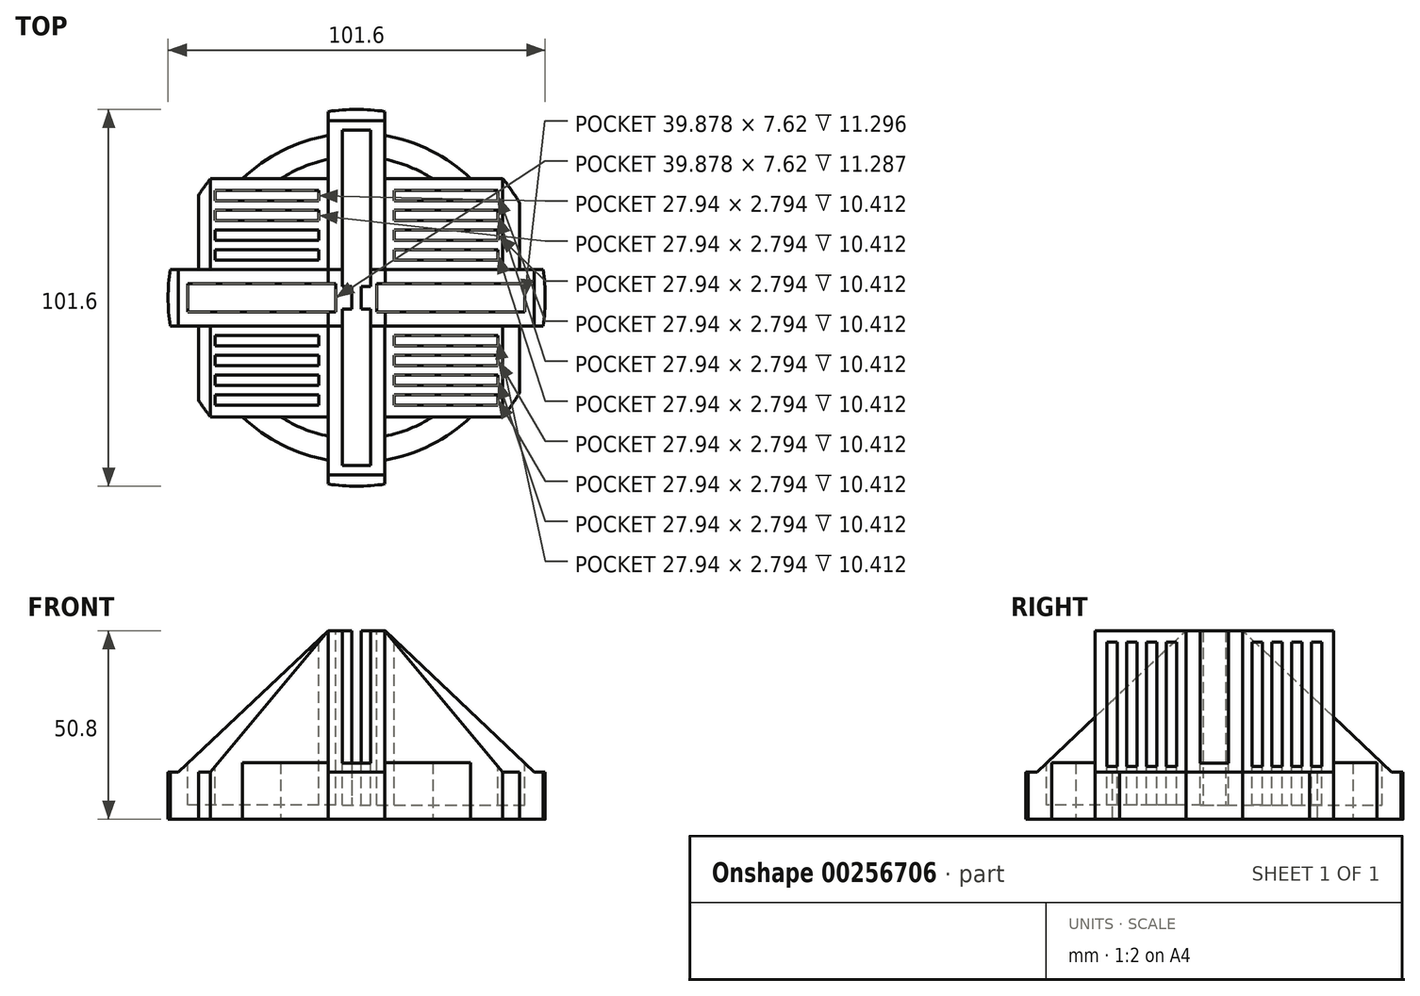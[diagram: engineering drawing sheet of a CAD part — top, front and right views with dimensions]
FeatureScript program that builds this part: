
annotation { "Feature Type Name" : "Feature", "Feature Type Description" : "" }
export const myFeature = defineFeature(function(context is Context, id is Id, definition is map)
    precondition{}
    {
        {
            var Q0;
            Q0=qCreatedBy(makeId("Top.planeOp"),FACE);
            cPlane(context, id + "F0", {"entities" : qUnion([Q0]), "cplaneType" : CPlaneType.OFFSET, "offset" : 50.8 * mm, "width" : 152.4 * mm, "height" : 152.4 * mm});
        }
        {
            var Q0;
            Q0=qCreatedBy(makeId("Top.planeOp"),FACE);
            var sketch = newSketch(context, id + "F1", { "sketchPlane" : qUnion([Q0])});
            skCircle(sketch, "E0", {"center": v(0, 0) * mm, "radius": 50.8 * mm});
            skArc(sketch, "E1", {"start": v(7.62, -43.8) * mm, "mid": v(26.54, -35.66) * mm, "end": v(39.77, -19.86) * mm});
            skArc(sketch, "E2", {"start": v(7.62, -37.33) * mm, "mid": v(38.1, 0) * mm, "end": v(7.62, 37.33) * mm});
            skCircle(sketch, "E3", {"center": v(0, 0) * mm, "radius": 25.4 * mm});
            skLineSegment(sketch, "E4", {"start": v(-7.62, -24.23) * mm, "end": v(-7.62, -50.23) * mm});
            skLineSegment(sketch, "E5", {"start": v(7.62, -24.23) * mm, "end": v(7.62, -50.23) * mm});
            skLineSegment(sketch, "E6", {"start": v(-7.62, 24.23) * mm, "end": v(-7.62, 50.23) * mm});
            skLineSegment(sketch, "E7", {"start": v(7.62, 24.23) * mm, "end": v(7.62, 50.23) * mm});
            skPoint(sketch, "E8.orphan", {"position": v(0, -25.4) * mm});
            skPoint(sketch, "E9.end.orphan", {"position": v(-3.8, -50.66) * mm});
            skArc(sketch, "E10.trimOffspring", {"start": v(-7.62, 37.33) * mm, "mid": v(-38.1, 0) * mm, "end": v(-7.62, -37.33) * mm});
            skArc(sketch, "E11.trimOffspring", {"start": v(-7.62, 43.8) * mm, "mid": v(-26.54, 35.66) * mm, "end": v(-39.77, 19.86) * mm});
            skArc(sketch, "E12", {"start": v(-7.62, -43.8) * mm, "mid": v(0, -44.45) * mm, "end": v(7.62, -43.8) * mm});
            skArc(sketch, "E13", {"start": v(-7.62, -37.33) * mm, "mid": v(0, -38.1) * mm, "end": v(7.62, -37.33) * mm});
            skCircle(sketch, "E14", {"center": v(0, 0) * mm, "radius": 31.75 * mm});
            skArc(sketch, "E15.trimOffspring", {"start": v(7.62, 43.8) * mm, "mid": v(0, 44.45) * mm, "end": v(-7.62, 43.8) * mm});
            skArc(sketch, "E16.trimOffspring", {"start": v(7.62, 37.33) * mm, "mid": v(0, 38.1) * mm, "end": v(-7.62, 37.33) * mm});
            skLineSegment(sketch, "E17", {"start": v(-7.62, -24.23) * mm, "end": v(-7.62, 24.23) * mm});
            skLineSegment(sketch, "E18", {"start": v(7.62, 24.23) * mm, "end": v(7.62, -24.23) * mm});
            skLineSegment(sketch, "E19", {"start": v(0, 7.62) * mm, "end": v(-50.23, 7.62) * mm});
            skLineSegment(sketch, "E20", {"start": v(0, 7.62) * mm, "end": v(50.23, 7.62) * mm});
            skLineSegment(sketch, "E21", {"start": v(0, -7.62) * mm, "end": v(50.23, -7.62) * mm});
            skLineSegment(sketch, "E22", {"start": v(0, -7.62) * mm, "end": v(-50.23, -7.62) * mm});
            skLineSegment(sketch, "E23", {"start": v(-17.78, 7.62) * mm, "end": v(7.62, -17.78) * mm});
            skLineSegment(sketch, "E24", {"start": v(-7.62, 17.78) * mm, "end": v(17.78, -7.62) * mm});
            skLineSegment(sketch, "E25", {"start": v(7.62, 17.78) * mm, "end": v(-17.78, -7.62) * mm});
            skLineSegment(sketch, "E26", {"start": v(17.78, 7.62) * mm, "end": v(-7.62, -17.78) * mm});
            skLineSegment(sketch, "E27", {"start": v(-7.62, -19.86) * mm, "end": v(-20.32, -19.86) * mm});
            skLineSegment(sketch, "E28", {"start": v(-20.32, -19.86) * mm, "end": v(-46.76, -19.86) * mm});
            skLineSegment(sketch, "E29.trimOffspring", {"start": v(-20.32, -32.1) * mm, "end": v(-20.32, -32.23) * mm});
            skPoint(sketch, "E30.start.orphan", {"position": v(-20.32, -7.62) * mm});
            skLineSegment(sketch, "E31", {"start": v(-7.62, -32.1) * mm, "end": v(-39.37, -32.1) * mm});
            skLineSegment(sketch, "E32", {"start": v(-7.62, 19.86) * mm, "end": v(-46.76, 19.86) * mm});
            skLineSegment(sketch, "E33", {"start": v(-7.62, 32.1) * mm, "end": v(-39.37, 32.1) * mm});
            skLineSegment(sketch, "E34", {"start": v(7.62, 32.1) * mm, "end": v(39.37, 32.1) * mm});
            skLineSegment(sketch, "E35", {"start": v(7.62, 19.86) * mm, "end": v(46.76, 19.86) * mm});
            skLineSegment(sketch, "E36", {"start": v(7.62, -19.86) * mm, "end": v(46.76, -19.86) * mm});
            skLineSegment(sketch, "E37", {"start": v(7.62, -32.1) * mm, "end": v(39.37, -32.1) * mm});
            skLineSegment(sketch, "E38", {"start": v(-42.64, 19.86) * mm, "end": v(-42.64, -19.86) * mm});
            skArc(sketch, "E39.trimOffspring", {"start": v(-39.77, -19.86) * mm, "mid": v(-26.54, -35.66) * mm, "end": v(-7.62, -43.8) * mm});
            skLineSegment(sketch, "E40", {"start": v(43.89, -19.86) * mm, "end": v(43.89, 19.86) * mm});
            skArc(sketch, "E41.trimOffspring", {"start": v(39.77, 19.86) * mm, "mid": v(26.54, 35.66) * mm, "end": v(7.62, 43.8) * mm});
            skSolve(sketch);
        }
        {
            var Q0;
            {var subQ5=sQuery(id+"F1.wireOp",EDGE,"E15.trimOffspring");Q0=makeQuery(id+"F1.imprint","IMPRINT",FACE,{"disambiguationData":[TD([[makeQuery(id+"F1.imprint","IMPRINT",EDGE,{"derivedFrom":subQ5}),-1.0]])]});}
            var Q1;
            {var subQ5=sQuery(id+"F1.wireOp",EDGE,"E12");Q1=makeQuery(id+"F1.imprint","IMPRINT",FACE,{"disambiguationData":[TD([[makeQuery(id+"F1.imprint","IMPRINT",EDGE,{"derivedFrom":subQ5}),-1.0]])]});}
            var Q2;
            {var subQ0=sQuery(id+"F1.wireOp",EDGE,"E32");var subQ6=sQuery(id+"F1.wireOp",EDGE,"E0");var subQ7=makeQuery(id+"F1.imprint","INTERSECT",VERTEX,{"derivedFrom":[subQ6,subQ0]});Q2=makeQuery(id+"F1.imprint","IMPRINT",FACE,{"disambiguationData":[TD([[makeQuery(id+"F1.imprint","IMPRINT",EDGE,{"disambiguationData":[TD([[subQ7,1.0]])],"derivedFrom":subQ6}),1.0]])]});}
            var Q3;
            {var subQ0=sQuery(id+"F1.wireOp",EDGE,"E19");var subQ1=sQuery(id+"F1.wireOp",EDGE,"E0");var subQ2=makeQuery(id+"F1.imprint","INTERSECT",VERTEX,{"derivedFrom":[subQ1,subQ0]});Q3=makeQuery(id+"F1.imprint","IMPRINT",FACE,{"disambiguationData":[TD([[makeQuery(id+"F1.imprint","IMPRINT",EDGE,{"disambiguationData":[TD([[subQ2,1.0]])],"derivedFrom":subQ1}),1.0]])]});}
            var Q4;
            {var subQ0=sQuery(id+"F1.wireOp",EDGE,"E19");var subQ1=sQuery(id+"F1.wireOp",EDGE,"E0");var subQ2=makeQuery(id+"F1.imprint","INTERSECT",VERTEX,{"derivedFrom":[subQ1,subQ0]});Q4=makeQuery(id+"F1.imprint","IMPRINT",FACE,{"disambiguationData":[TD([[makeQuery(id+"F1.imprint","IMPRINT",EDGE,{"disambiguationData":[TD([[subQ2,-1.0]])],"derivedFrom":subQ1}),1.0]])]});}
            var Q5;
            {var subQ0=sQuery(id+"F1.wireOp",EDGE,"E22");var subQ1=sQuery(id+"F1.wireOp",EDGE,"E0");var subQ2=makeQuery(id+"F1.imprint","INTERSECT",VERTEX,{"derivedFrom":[subQ1,subQ0]});Q5=makeQuery(id+"F1.imprint","IMPRINT",FACE,{"disambiguationData":[TD([[makeQuery(id+"F1.imprint","IMPRINT",EDGE,{"disambiguationData":[TD([[subQ2,-1.0]])],"derivedFrom":subQ1}),1.0]])]});}
            var Q6;
            {var subQ0=sQuery(id+"F1.wireOp",EDGE,"E28");var subQ4=sQuery(id+"F1.wireOp",EDGE,"E0");var subQ5=makeQuery(id+"F1.imprint","INTERSECT",VERTEX,{"derivedFrom":[subQ4,subQ0]});Q6=makeQuery(id+"F1.imprint","IMPRINT",FACE,{"disambiguationData":[TD([[makeQuery(id+"F1.imprint","IMPRINT",EDGE,{"disambiguationData":[TD([[subQ5,-1.0]])],"derivedFrom":subQ4}),1.0]])]});}
            var Q7;
            {var subQ1=sQuery(id+"F1.wireOp",EDGE,"E0");var subQ6=sQuery(id+"F1.wireOp",EDGE,"E34");var subQ8=makeQuery(id+"F1.imprint","INTERSECT",VERTEX,{"derivedFrom":[subQ1,subQ6]});Q7=makeQuery(id+"F1.imprint","IMPRINT",FACE,{"disambiguationData":[TD([[makeQuery(id+"F1.imprint","IMPRINT",EDGE,{"disambiguationData":[TD([[subQ8,1.0]])],"derivedFrom":subQ1}),1.0]])]});}
            var Q8;
            {var subQ0=sQuery(id+"F1.wireOp",EDGE,"E20");var subQ1=sQuery(id+"F1.wireOp",EDGE,"E0");var subQ2=makeQuery(id+"F1.imprint","INTERSECT",VERTEX,{"derivedFrom":[subQ1,subQ0]});Q8=makeQuery(id+"F1.imprint","IMPRINT",FACE,{"disambiguationData":[TD([[makeQuery(id+"F1.imprint","IMPRINT",EDGE,{"disambiguationData":[TD([[subQ2,-1.0]])],"derivedFrom":subQ1}),1.0]])]});}
            var Q9;
            {var subQ1=sQuery(id+"F1.wireOp",EDGE,"E0");var subQ5=sQuery(id+"F1.wireOp",EDGE,"E20");var subQ6=makeQuery(id+"F1.imprint","INTERSECT",VERTEX,{"derivedFrom":[subQ1,subQ5]});Q9=makeQuery(id+"F1.imprint","IMPRINT",FACE,{"disambiguationData":[TD([[makeQuery(id+"F1.imprint","IMPRINT",EDGE,{"disambiguationData":[TD([[subQ6,1.0]])],"derivedFrom":subQ1}),1.0]])]});}
            var Q10;
            {var subQ0=sQuery(id+"F1.wireOp",EDGE,"E21");var subQ1=sQuery(id+"F1.wireOp",EDGE,"E0");var subQ2=makeQuery(id+"F1.imprint","INTERSECT",VERTEX,{"derivedFrom":[subQ1,subQ0]});Q10=makeQuery(id+"F1.imprint","IMPRINT",FACE,{"disambiguationData":[TD([[makeQuery(id+"F1.imprint","IMPRINT",EDGE,{"disambiguationData":[TD([[subQ2,1.0]])],"derivedFrom":subQ1}),1.0]])]});}
            var Q11;
            {var subQ0=sQuery(id+"F1.wireOp",EDGE,"E36");var subQ1=sQuery(id+"F1.wireOp",EDGE,"E0");var subQ2=makeQuery(id+"F1.imprint","INTERSECT",VERTEX,{"derivedFrom":[subQ1,subQ0]});Q11=makeQuery(id+"F1.imprint","IMPRINT",FACE,{"disambiguationData":[TD([[makeQuery(id+"F1.imprint","IMPRINT",EDGE,{"disambiguationData":[TD([[subQ2,1.0]])],"derivedFrom":subQ1}),1.0]])]});}
            var Q12;
            {var subQ0=sQuery(id+"F1.wireOp",EDGE,"E4");var subQ1=sQuery(id+"F1.wireOp",EDGE,"E0");var subQ2=makeQuery(id+"F1.imprint","INTERSECT",VERTEX,{"derivedFrom":[subQ1,subQ0]});Q12=makeQuery(id+"F1.imprint","IMPRINT",FACE,{"disambiguationData":[TD([[makeQuery(id+"F1.imprint","IMPRINT",EDGE,{"disambiguationData":[TD([[subQ2,1.0]])],"derivedFrom":subQ1}),1.0]])]});}
            var Q13;
            {var subQ0=sQuery(id+"F1.wireOp",EDGE,"E6");var subQ1=sQuery(id+"F1.wireOp",EDGE,"E0");var subQ2=makeQuery(id+"F1.imprint","INTERSECT",VERTEX,{"derivedFrom":[subQ1,subQ0]});Q13=makeQuery(id+"F1.imprint","IMPRINT",FACE,{"disambiguationData":[TD([[makeQuery(id+"F1.imprint","IMPRINT",EDGE,{"disambiguationData":[TD([[subQ2,-1.0]])],"derivedFrom":subQ1}),1.0]])]});}
            var Q14;
            {var subQ0=sQuery(id+"F1.wireOp",EDGE,"E7");var subQ1=sQuery(id+"F1.wireOp",EDGE,"E0");var subQ2=makeQuery(id+"F1.imprint","INTERSECT",VERTEX,{"derivedFrom":[subQ1,subQ0]});Q14=makeQuery(id+"F1.imprint","IMPRINT",FACE,{"disambiguationData":[TD([[makeQuery(id+"F1.imprint","IMPRINT",EDGE,{"disambiguationData":[TD([[subQ2,1.0]])],"derivedFrom":subQ1}),1.0]])]});}
            var Q15;
            {var subQ0=sQuery(id+"F1.wireOp",EDGE,"E5");var subQ1=sQuery(id+"F1.wireOp",EDGE,"E0");var subQ2=makeQuery(id+"F1.imprint","INTERSECT",VERTEX,{"derivedFrom":[subQ1,subQ0]});Q15=makeQuery(id+"F1.imprint","IMPRINT",FACE,{"disambiguationData":[TD([[makeQuery(id+"F1.imprint","IMPRINT",EDGE,{"disambiguationData":[TD([[subQ2,-1.0]])],"derivedFrom":subQ1}),1.0]])]});}
            extrude(context, id + "F2", {"entities" : qUnion([Q0, Q1, Q2, Q3, Q4, Q5, Q6, Q7, Q8, Q9, Q10, Q11, Q12, Q13, Q14, Q15]), "depth" : 12.7 * mm});
        }
        {
            var Q0;
            {var subQ0=sQuery(id+"F1.wireOp",EDGE,"E10.trimOffspring");Q0=makeQuery(id+"F1.imprint","IMPRINT",FACE,{"disambiguationData":[TD([[makeQuery(id+"F1.imprint","IMPRINT",EDGE,{"derivedFrom":subQ0}),-1.0]])]});}
            var Q1;
            {var subQ0=sQuery(id+"F1.wireOp",EDGE,"E1");Q1=makeQuery(id+"F1.imprint","IMPRINT",FACE,{"disambiguationData":[TD([[makeQuery(id+"F1.imprint","IMPRINT",EDGE,{"derivedFrom":subQ0}),1.0]])]});}
            var Q2;
            {var subQ2=sQuery(id+"F1.wireOp",EDGE,"E15.trimOffspring");Q2=makeQuery(id+"F1.imprint","IMPRINT",FACE,{"disambiguationData":[TD([[makeQuery(id+"F1.imprint","IMPRINT",EDGE,{"derivedFrom":subQ2}),1.0]])]});}
            var Q3;
            {var subQ2=sQuery(id+"F1.wireOp",EDGE,"E12");Q3=makeQuery(id+"F1.imprint","IMPRINT",FACE,{"disambiguationData":[TD([[makeQuery(id+"F1.imprint","IMPRINT",EDGE,{"derivedFrom":subQ2}),1.0]])]});}
            var Q4;
            {var subQ0=sQuery(id+"F1.wireOp",EDGE,"E10.trimOffspring");var subQ5=sQuery(id+"F1.wireOp",EDGE,"KU0cdiGB-8eOj-Trs3-v5YD-3LzdnCRRimhK");var subQ6=makeQuery(id+"F1.imprint","INTERSECT",VERTEX,{"derivedFrom":[subQ0,subQ5]});Q4=makeQuery(id+"F1.imprint","IMPRINT",FACE,{"disambiguationData":[TD([[makeQuery(id+"F1.imprint","IMPRINT",EDGE,{"disambiguationData":[TD([[subQ6,-1.0]])],"derivedFrom":subQ5}),-1.0]])]});}
            var Q5;
            {var subQ0=sQuery(id+"F1.wireOp",EDGE,"KU0cdiGB-8eOj-Trs3-v5YD-3LzdnCRRimhK");var subQ1=sQuery(id+"F1.wireOp",EDGE,"E10.trimOffspring");var subQ2=makeQuery(id+"F1.imprint","INTERSECT",VERTEX,{"derivedFrom":[subQ1,subQ0]});Q5=makeQuery(id+"F1.imprint","IMPRINT",FACE,{"disambiguationData":[TD([[makeQuery(id+"F1.imprint","IMPRINT",EDGE,{"disambiguationData":[TD([[subQ2,-1.0]])],"derivedFrom":subQ1}),-1.0]])]});}
            var Q6;
            {var subQ0=sQuery(id+"F1.wireOp",EDGE,"n5LII22h-w08l-qE72-yfr9-18N67uZxNTdQ");var subQ1=sQuery(id+"F1.wireOp",EDGE,"E10.trimOffspring");var subQ2=makeQuery(id+"F1.imprint","INTERSECT",VERTEX,{"derivedFrom":[subQ1,subQ0]});Q6=makeQuery(id+"F1.imprint","IMPRINT",FACE,{"disambiguationData":[TD([[makeQuery(id+"F1.imprint","IMPRINT",EDGE,{"disambiguationData":[TD([[subQ2,-1.0]])],"derivedFrom":subQ1}),-1.0]])]});}
            var Q7;
            {var subQ0=sQuery(id+"F1.wireOp",EDGE,"E19");var subQ1=sQuery(id+"F1.wireOp",EDGE,"E10.trimOffspring");var subQ2=makeQuery(id+"F1.imprint","INTERSECT",VERTEX,{"derivedFrom":[subQ1,subQ0]});Q7=makeQuery(id+"F1.imprint","IMPRINT",FACE,{"disambiguationData":[TD([[makeQuery(id+"F1.imprint","IMPRINT",EDGE,{"disambiguationData":[TD([[subQ2,-1.0]])],"derivedFrom":subQ1}),-1.0]])]});}
            var Q8;
            {var subQ0=sQuery(id+"F1.wireOp",EDGE,"E22");var subQ1=sQuery(id+"F1.wireOp",EDGE,"E10.trimOffspring");var subQ2=makeQuery(id+"F1.imprint","INTERSECT",VERTEX,{"derivedFrom":[subQ1,subQ0]});Q8=makeQuery(id+"F1.imprint","IMPRINT",FACE,{"disambiguationData":[TD([[makeQuery(id+"F1.imprint","IMPRINT",EDGE,{"disambiguationData":[TD([[subQ2,-1.0]])],"derivedFrom":subQ1}),-1.0]])]});}
            var Q9;
            {var subQ0=sQuery(id+"F1.wireOp",EDGE,"E28");var subQ1=sQuery(id+"F1.wireOp",EDGE,"E10.trimOffspring");var subQ2=makeQuery(id+"F1.imprint","INTERSECT",VERTEX,{"derivedFrom":[subQ1,subQ0]});Q9=makeQuery(id+"F1.imprint","IMPRINT",FACE,{"disambiguationData":[TD([[makeQuery(id+"F1.imprint","IMPRINT",EDGE,{"disambiguationData":[TD([[subQ2,-1.0]])],"derivedFrom":subQ1}),-1.0]])]});}
            var Q10;
            {var subQ1=sQuery(id+"F1.wireOp",EDGE,"E10.trimOffspring");var subQ5=sQuery(id+"F1.wireOp",EDGE,"E25");var subQ6=makeQuery(id+"F1.imprint","INTERSECT",VERTEX,{"derivedFrom":[subQ1,subQ5]});Q10=makeQuery(id+"F1.imprint","IMPRINT",FACE,{"disambiguationData":[TD([[makeQuery(id+"F1.imprint","IMPRINT",EDGE,{"disambiguationData":[TD([[subQ6,-1.0]])],"derivedFrom":subQ1}),-1.0]])]});}
            var Q11;
            {var subQ0=sQuery(id+"F1.wireOp",EDGE,"E31");var subQ1=sQuery(id+"F1.wireOp",EDGE,"E11.trimOffspring");var subQ2=makeQuery(id+"F1.imprint","INTERSECT",VERTEX,{"derivedFrom":[subQ1,subQ0]});Q11=makeQuery(id+"F1.imprint","IMPRINT",FACE,{"disambiguationData":[TD([[makeQuery(id+"F1.imprint","IMPRINT",EDGE,{"disambiguationData":[TD([[subQ2,-1.0]])],"derivedFrom":subQ1}),1.0]])]});}
            var Q12;
            {var subQ0=sQuery(id+"F1.wireOp",EDGE,"E26");var subQ1=sQuery(id+"F1.wireOp",EDGE,"E10.trimOffspring");var subQ2=makeQuery(id+"F1.imprint","INTERSECT",VERTEX,{"derivedFrom":[subQ1,subQ0]});Q12=makeQuery(id+"F1.imprint","IMPRINT",FACE,{"disambiguationData":[TD([[makeQuery(id+"F1.imprint","IMPRINT",EDGE,{"disambiguationData":[TD([[subQ2,-1.0]])],"derivedFrom":subQ1}),-1.0]])]});}
            var Q13;
            {var subQ0=sQuery(id+"F1.wireOp",EDGE,"E32");var subQ1=sQuery(id+"F1.wireOp",EDGE,"E10.trimOffspring");var subQ2=makeQuery(id+"F1.imprint","INTERSECT",VERTEX,{"derivedFrom":[subQ1,subQ0]});Q13=makeQuery(id+"F1.imprint","IMPRINT",FACE,{"disambiguationData":[TD([[makeQuery(id+"F1.imprint","IMPRINT",EDGE,{"disambiguationData":[TD([[subQ2,-1.0]])],"derivedFrom":subQ1}),-1.0]])]});}
            var Q14;
            {var subQ0=sQuery(id+"F1.wireOp",EDGE,"E33");var subQ1=sQuery(id+"F1.wireOp",EDGE,"E10.trimOffspring");var subQ2=makeQuery(id+"F1.imprint","INTERSECT",VERTEX,{"derivedFrom":[subQ1,subQ0]});Q14=makeQuery(id+"F1.imprint","IMPRINT",FACE,{"disambiguationData":[TD([[makeQuery(id+"F1.imprint","IMPRINT",EDGE,{"disambiguationData":[TD([[subQ2,-1.0]])],"derivedFrom":subQ1}),-1.0]])]});}
            var Q15;
            {var subQ0=sQuery(id+"F1.wireOp",EDGE,"E10.trimOffspring");var subQ5=sQuery(id+"F1.wireOp",EDGE,"E33");var subQ7=makeQuery(id+"F1.imprint","INTERSECT",VERTEX,{"derivedFrom":[subQ0,subQ5]});Q15=makeQuery(id+"F1.imprint","IMPRINT",FACE,{"disambiguationData":[TD([[makeQuery(id+"F1.imprint","IMPRINT",EDGE,{"disambiguationData":[TD([[subQ7,-1.0]])],"derivedFrom":subQ5}),-1.0]])]});}
            var Q16;
            {var subQ0=sQuery(id+"F1.wireOp",EDGE,"E35");var subQ1=sQuery(id+"F1.wireOp",EDGE,"E2");var subQ2=makeQuery(id+"F1.imprint","INTERSECT",VERTEX,{"derivedFrom":[subQ1,subQ0]});Q16=makeQuery(id+"F1.imprint","IMPRINT",FACE,{"disambiguationData":[TD([[makeQuery(id+"F1.imprint","IMPRINT",EDGE,{"disambiguationData":[TD([[subQ2,-1.0]])],"derivedFrom":subQ1}),-1.0]])]});}
            var Q17;
            {var subQ0=sQuery(id+"F1.wireOp",EDGE,"E20");var subQ6=sQuery(id+"F1.wireOp",EDGE,"E2");var subQ8=makeQuery(id+"F1.imprint","INTERSECT",VERTEX,{"derivedFrom":[subQ6,subQ0]});Q17=makeQuery(id+"F1.imprint","IMPRINT",FACE,{"disambiguationData":[TD([[makeQuery(id+"F1.imprint","IMPRINT",EDGE,{"disambiguationData":[TD([[subQ8,-1.0]])],"derivedFrom":subQ6}),-1.0]])]});}
            var Q18;
            {var subQ0=sQuery(id+"F1.wireOp",EDGE,"18cd6810-feed-407b-96fd-876ede30ebc9.trimOffspring");Q18=makeQuery(id+"F1.imprint","IMPRINT",FACE,{"disambiguationData":[TD([[makeQuery(id+"F1.imprint","IMPRINT",EDGE,{"derivedFrom":subQ0}),1.0]])]});}
            var Q19;
            {var subQ0=sQuery(id+"F1.wireOp",EDGE,"E36");var subQ2=sQuery(id+"F1.wireOp",EDGE,"E2");var subQ3=makeQuery(id+"F1.imprint","INTERSECT",VERTEX,{"derivedFrom":[subQ2,subQ0]});Q19=makeQuery(id+"F1.imprint","IMPRINT",FACE,{"disambiguationData":[TD([[makeQuery(id+"F1.imprint","IMPRINT",EDGE,{"disambiguationData":[TD([[subQ3,-1.0]])],"derivedFrom":subQ2}),-1.0]])]});}
            var Q20;
            {var subQ0=sQuery(id+"F1.wireOp",EDGE,"E21");var subQ1=sQuery(id+"F1.wireOp",EDGE,"E2");var subQ2=makeQuery(id+"F1.imprint","INTERSECT",VERTEX,{"derivedFrom":[subQ1,subQ0]});Q20=makeQuery(id+"F1.imprint","IMPRINT",FACE,{"disambiguationData":[TD([[makeQuery(id+"F1.imprint","IMPRINT",EDGE,{"disambiguationData":[TD([[subQ2,-1.0]])],"derivedFrom":subQ1}),-1.0]])]});}
            var Q21;
            {var subQ1=sQuery(id+"F1.wireOp",EDGE,"E2");var subQ3=sQuery(id+"F1.wireOp",EDGE,"E34");var subQ4=makeQuery(id+"F1.imprint","INTERSECT",VERTEX,{"derivedFrom":[subQ1,subQ3]});Q21=makeQuery(id+"F1.imprint","IMPRINT",FACE,{"disambiguationData":[TD([[makeQuery(id+"F1.imprint","IMPRINT",EDGE,{"disambiguationData":[TD([[subQ4,-1.0]])],"derivedFrom":subQ3}),1.0]])]});}
            extrude(context, id + "F3", {"entities" : qUnion([Q0, Q1, Q2, Q3, Q4, Q5, Q6, Q7, Q8, Q9, Q10, Q11, Q12, Q13, Q14, Q15, Q16, Q17, Q18, Q19, Q20, Q21]), "operationType" : NewBodyOperationType.ADD, "depth" : 25.4 * mm});
        }
        {
            var Q0;
            {var subQ0=sQuery(id+"F1.wireOp",EDGE,"E13");Q0=makeQuery(id+"F1.imprint","IMPRINT",FACE,{"disambiguationData":[TD([[makeQuery(id+"F1.imprint","IMPRINT",EDGE,{"derivedFrom":subQ0}),1.0]])]});}
            var Q1;
            {var subQ0=sQuery(id+"F1.wireOp",EDGE,"E10.trimOffspring");Q1=makeQuery(id+"F1.imprint","IMPRINT",FACE,{"disambiguationData":[TD([[makeQuery(id+"F1.imprint","IMPRINT",EDGE,{"derivedFrom":subQ0}),1.0]])]});}
            var Q2;
            {var subQ0=sQuery(id+"F1.wireOp",EDGE,"E2");Q2=makeQuery(id+"F1.imprint","IMPRINT",FACE,{"disambiguationData":[TD([[makeQuery(id+"F1.imprint","IMPRINT",EDGE,{"derivedFrom":subQ0}),1.0]])]});}
            var Q3;
            {var subQ0=sQuery(id+"F1.wireOp",EDGE,"E16.trimOffspring");Q3=makeQuery(id+"F1.imprint","IMPRINT",FACE,{"disambiguationData":[TD([[makeQuery(id+"F1.imprint","IMPRINT",EDGE,{"derivedFrom":subQ0}),1.0]])]});}
            var Q4;
            {var subQ0=sQuery(id+"F1.wireOp",EDGE,"n5LII22h-w08l-qE72-yfr9-18N67uZxNTdQ");var subQ1=sQuery(id+"F1.wireOp",EDGE,"E10.trimOffspring");var subQ2=makeQuery(id+"F1.imprint","INTERSECT",VERTEX,{"derivedFrom":[subQ1,subQ0]});Q4=makeQuery(id+"F1.imprint","IMPRINT",FACE,{"disambiguationData":[TD([[makeQuery(id+"F1.imprint","IMPRINT",EDGE,{"disambiguationData":[TD([[subQ2,-1.0]])],"derivedFrom":subQ1}),1.0]])]});}
            var Q5;
            {var subQ0=sQuery(id+"F1.wireOp",EDGE,"KU0cdiGB-8eOj-Trs3-v5YD-3LzdnCRRimhK");var subQ1=sQuery(id+"F1.wireOp",EDGE,"E10.trimOffspring");var subQ2=makeQuery(id+"F1.imprint","INTERSECT",VERTEX,{"derivedFrom":[subQ1,subQ0]});Q5=makeQuery(id+"F1.imprint","IMPRINT",FACE,{"disambiguationData":[TD([[makeQuery(id+"F1.imprint","IMPRINT",EDGE,{"disambiguationData":[TD([[subQ2,-1.0]])],"derivedFrom":subQ1}),1.0]])]});}
            var Q6;
            {var subQ1=sQuery(id+"F1.wireOp",EDGE,"E6");var subQ3=sQuery(id+"F1.wireOp",EDGE,"E14");var subQ4=makeQuery(id+"F1.imprint","INTERSECT",VERTEX,{"derivedFrom":[subQ1,subQ3]});Q6=makeQuery(id+"F1.imprint","IMPRINT",FACE,{"disambiguationData":[TD([[makeQuery(id+"F1.imprint","IMPRINT",EDGE,{"disambiguationData":[TD([[subQ4,-1.0]])],"derivedFrom":subQ3}),-1.0]])]});}
            var Q7;
            {var subQ0=sQuery(id+"F1.wireOp",EDGE,"E7");var subQ5=sQuery(id+"F1.wireOp",EDGE,"E14");var subQ6=makeQuery(id+"F1.imprint","INTERSECT",VERTEX,{"derivedFrom":[subQ0,subQ5]});Q7=makeQuery(id+"F1.imprint","IMPRINT",FACE,{"disambiguationData":[TD([[makeQuery(id+"F1.imprint","IMPRINT",EDGE,{"disambiguationData":[TD([[subQ6,1.0]])],"derivedFrom":subQ5}),-1.0]])]});}
            var Q8;
            {var subQ0=sQuery(id+"F1.wireOp",EDGE,"E19");var subQ1=sQuery(id+"F1.wireOp",EDGE,"E10.trimOffspring");var subQ2=makeQuery(id+"F1.imprint","INTERSECT",VERTEX,{"derivedFrom":[subQ1,subQ0]});Q8=makeQuery(id+"F1.imprint","IMPRINT",FACE,{"disambiguationData":[TD([[makeQuery(id+"F1.imprint","IMPRINT",EDGE,{"disambiguationData":[TD([[subQ2,-1.0]])],"derivedFrom":subQ1}),1.0]])]});}
            var Q9;
            {var subQ0=sQuery(id+"F1.wireOp",EDGE,"E22");var subQ1=sQuery(id+"F1.wireOp",EDGE,"E10.trimOffspring");var subQ2=makeQuery(id+"F1.imprint","INTERSECT",VERTEX,{"derivedFrom":[subQ1,subQ0]});Q9=makeQuery(id+"F1.imprint","IMPRINT",FACE,{"disambiguationData":[TD([[makeQuery(id+"F1.imprint","IMPRINT",EDGE,{"disambiguationData":[TD([[subQ2,-1.0]])],"derivedFrom":subQ1}),1.0]])]});}
            var Q10;
            {var subQ0=sQuery(id+"F1.wireOp",EDGE,"E25");var subQ1=sQuery(id+"F1.wireOp",EDGE,"E10.trimOffspring");var subQ2=makeQuery(id+"F1.imprint","INTERSECT",VERTEX,{"derivedFrom":[subQ1,subQ0]});Q10=makeQuery(id+"F1.imprint","IMPRINT",FACE,{"disambiguationData":[TD([[makeQuery(id+"F1.imprint","IMPRINT",EDGE,{"disambiguationData":[TD([[subQ2,-1.0]])],"derivedFrom":subQ1}),1.0]])]});}
            var Q11;
            {var subQ3=sQuery(id+"F1.wireOp",EDGE,"E14");var subQ7=sQuery(id+"F1.wireOp",EDGE,"E4");var subQ8=makeQuery(id+"F1.imprint","INTERSECT",VERTEX,{"derivedFrom":[subQ7,subQ3]});Q11=makeQuery(id+"F1.imprint","IMPRINT",FACE,{"disambiguationData":[TD([[makeQuery(id+"F1.imprint","IMPRINT",EDGE,{"disambiguationData":[TD([[subQ8,-1.0]])],"derivedFrom":subQ7}),-1.0]])]});}
            var Q12;
            {var subQ1=sQuery(id+"F1.wireOp",EDGE,"E2");var subQ5=sQuery(id+"F1.wireOp",EDGE,"dChad7VG-r3lr-Y0ra-zuCQ-UW0r8UzcO7aT");var subQ6=makeQuery(id+"F1.imprint","INTERSECT",VERTEX,{"derivedFrom":[subQ1,subQ5]});Q12=makeQuery(id+"F1.imprint","IMPRINT",FACE,{"disambiguationData":[TD([[makeQuery(id+"F1.imprint","IMPRINT",EDGE,{"disambiguationData":[TD([[subQ6,-1.0]])],"derivedFrom":subQ1}),1.0]])]});}
            var Q13;
            {var subQ0=sQuery(id+"F1.wireOp",EDGE,"E23");var subQ1=sQuery(id+"F1.wireOp",EDGE,"E2");var subQ2=makeQuery(id+"F1.imprint","INTERSECT",VERTEX,{"derivedFrom":[subQ1,subQ0]});Q13=makeQuery(id+"F1.imprint","IMPRINT",FACE,{"disambiguationData":[TD([[makeQuery(id+"F1.imprint","IMPRINT",EDGE,{"disambiguationData":[TD([[subQ2,-1.0]])],"derivedFrom":subQ1}),1.0]])]});}
            var Q14;
            {var subQ0=sQuery(id+"F1.wireOp",EDGE,"E24");var subQ1=sQuery(id+"F1.wireOp",EDGE,"E2");var subQ2=makeQuery(id+"F1.imprint","INTERSECT",VERTEX,{"derivedFrom":[subQ1,subQ0]});Q14=makeQuery(id+"F1.imprint","IMPRINT",FACE,{"disambiguationData":[TD([[makeQuery(id+"F1.imprint","IMPRINT",EDGE,{"disambiguationData":[TD([[subQ2,-1.0]])],"derivedFrom":subQ1}),1.0]])]});}
            var Q15;
            {var subQ0=sQuery(id+"F1.wireOp",EDGE,"E21");var subQ1=sQuery(id+"F1.wireOp",EDGE,"E2");var subQ2=makeQuery(id+"F1.imprint","INTERSECT",VERTEX,{"derivedFrom":[subQ1,subQ0]});Q15=makeQuery(id+"F1.imprint","IMPRINT",FACE,{"disambiguationData":[TD([[makeQuery(id+"F1.imprint","IMPRINT",EDGE,{"disambiguationData":[TD([[subQ2,-1.0]])],"derivedFrom":subQ1}),1.0]])]});}
            var Q16;
            {var subQ0=sQuery(id+"F1.wireOp",EDGE,"E20");var subQ1=sQuery(id+"F1.wireOp",EDGE,"E2");var subQ2=makeQuery(id+"F1.imprint","INTERSECT",VERTEX,{"derivedFrom":[subQ1,subQ0]});Q16=makeQuery(id+"F1.imprint","IMPRINT",FACE,{"disambiguationData":[TD([[makeQuery(id+"F1.imprint","IMPRINT",EDGE,{"disambiguationData":[TD([[subQ2,-1.0]])],"derivedFrom":subQ1}),1.0]])]});}
            var Q17;
            {var subQ0=sQuery(id+"F1.wireOp",EDGE,"SVIod6WE-LFFt-Ms97-owyS-8ShU65W6W8it");var subQ1=sQuery(id+"F1.wireOp",EDGE,"E2");var subQ2=makeQuery(id+"F1.imprint","INTERSECT",VERTEX,{"derivedFrom":[subQ1,subQ0]});Q17=makeQuery(id+"F1.imprint","IMPRINT",FACE,{"disambiguationData":[TD([[makeQuery(id+"F1.imprint","IMPRINT",EDGE,{"disambiguationData":[TD([[subQ2,-1.0]])],"derivedFrom":subQ1}),1.0]])]});}
            var Q18;
            {var subQ0=sQuery(id+"F1.wireOp",EDGE,"E25");var subQ1=sQuery(id+"F1.wireOp",EDGE,"E14");var subQ2=makeQuery(id+"F1.imprint","INTERSECT",VERTEX,{"derivedFrom":[subQ1,subQ0]});Q18=makeQuery(id+"F1.imprint","IMPRINT",FACE,{"disambiguationData":[TD([[makeQuery(id+"F1.imprint","IMPRINT",EDGE,{"disambiguationData":[TD([[subQ2,-1.0]])],"derivedFrom":subQ1}),-1.0]])]});}
            var Q19;
            {var subQ0=sQuery(id+"F1.wireOp",EDGE,"E30");var subQ1=sQuery(id+"F1.wireOp",EDGE,"E14");var subQ2=makeQuery(id+"F1.imprint","INTERSECT",VERTEX,{"derivedFrom":[subQ1,subQ0]});Q19=makeQuery(id+"F1.imprint","IMPRINT",FACE,{"disambiguationData":[TD([[makeQuery(id+"F1.imprint","IMPRINT",EDGE,{"disambiguationData":[TD([[subQ2,-1.0]])],"derivedFrom":subQ1}),-1.0]])]});}
            var Q20;
            {var subQ5=sQuery(id+"F1.wireOp",EDGE,"E29.trimOffspring");Q20=makeQuery(id+"F1.imprint","IMPRINT",FACE,{"disambiguationData":[TD([[makeQuery(id+"F1.imprint","IMPRINT",EDGE,{"derivedFrom":subQ5}),1.0]])]});}
            var Q21;
            {var subQ1=sQuery(id+"F1.wireOp",EDGE,"E2");var subQ7=sQuery(id+"F1.wireOp",EDGE,"E37");var subQ9=makeQuery(id+"F1.imprint","INTERSECT",VERTEX,{"derivedFrom":[subQ1,subQ7]});Q21=makeQuery(id+"F1.imprint","IMPRINT",FACE,{"disambiguationData":[TD([[makeQuery(id+"F1.imprint","IMPRINT",EDGE,{"disambiguationData":[TD([[subQ9,-1.0]])],"derivedFrom":subQ1}),1.0]])]});}
            extrude(context, id + "F4", {"entities" : qUnion([Q0, Q1, Q2, Q3, Q4, Q5, Q6, Q7, Q8, Q9, Q10, Q11, Q12, Q13, Q14, Q15, Q16, Q17, Q18, Q19, Q20, Q21]), "operationType" : NewBodyOperationType.ADD, "depth" : 38.1 * mm});
        }
        {
            var Q0;
            {var subQ0=sQuery(id+"F1.wireOp",EDGE,"E6");var subQ1=sQuery(id+"F1.wireOp",EDGE,"E3");var subQ2=makeQuery(id+"F1.imprint","INTERSECT",VERTEX,{"derivedFrom":[subQ1,subQ0]});Q0=makeQuery(id+"F1.imprint","IMPRINT",FACE,{"disambiguationData":[TD([[makeQuery(id+"F1.imprint","IMPRINT",EDGE,{"disambiguationData":[TD([[subQ2,1.0]])],"derivedFrom":subQ1}),-1.0]])]});}
            var Q1;
            {var subQ0=sQuery(id+"F1.wireOp",EDGE,"E4");var subQ1=sQuery(id+"F1.wireOp",EDGE,"E3");var subQ2=makeQuery(id+"F1.imprint","INTERSECT",VERTEX,{"derivedFrom":[subQ1,subQ0]});Q1=makeQuery(id+"F1.imprint","IMPRINT",FACE,{"disambiguationData":[TD([[makeQuery(id+"F1.imprint","IMPRINT",EDGE,{"disambiguationData":[TD([[subQ2,-1.0]])],"derivedFrom":subQ1}),-1.0]])]});}
            var Q2;
            {var subQ0=sQuery(id+"F1.wireOp",EDGE,"E5");var subQ1=sQuery(id+"F1.wireOp",EDGE,"E3");var subQ2=makeQuery(id+"F1.imprint","INTERSECT",VERTEX,{"derivedFrom":[subQ1,subQ0]});Q2=makeQuery(id+"F1.imprint","IMPRINT",FACE,{"disambiguationData":[TD([[makeQuery(id+"F1.imprint","IMPRINT",EDGE,{"disambiguationData":[TD([[subQ2,-1.0]])],"derivedFrom":subQ1}),-1.0]])]});}
            var Q3;
            {var subQ0=sQuery(id+"F1.wireOp",EDGE,"E7");var subQ5=sQuery(id+"F1.wireOp",EDGE,"E14");var subQ6=makeQuery(id+"F1.imprint","INTERSECT",VERTEX,{"derivedFrom":[subQ0,subQ5]});Q3=makeQuery(id+"F1.imprint","IMPRINT",FACE,{"disambiguationData":[TD([[makeQuery(id+"F1.imprint","IMPRINT",EDGE,{"disambiguationData":[TD([[subQ6,1.0]])],"derivedFrom":subQ5}),1.0]])]});}
            var Q4;
            {var subQ0=sQuery(id+"F1.wireOp",EDGE,"E19");var subQ1=sQuery(id+"F1.wireOp",EDGE,"E3");var subQ2=makeQuery(id+"F1.imprint","INTERSECT",VERTEX,{"derivedFrom":[subQ1,subQ0]});Q4=makeQuery(id+"F1.imprint","IMPRINT",FACE,{"disambiguationData":[TD([[makeQuery(id+"F1.imprint","IMPRINT",EDGE,{"disambiguationData":[TD([[subQ2,-1.0]])],"derivedFrom":subQ1}),-1.0]])]});}
            var Q5;
            {var subQ0=sQuery(id+"F1.wireOp",EDGE,"E6");var subQ5=sQuery(id+"F1.wireOp",EDGE,"E14");var subQ6=makeQuery(id+"F1.imprint","INTERSECT",VERTEX,{"derivedFrom":[subQ0,subQ5]});Q5=makeQuery(id+"F1.imprint","IMPRINT",FACE,{"disambiguationData":[TD([[makeQuery(id+"F1.imprint","IMPRINT",EDGE,{"disambiguationData":[TD([[subQ6,-1.0]])],"derivedFrom":subQ5}),1.0]])]});}
            var Q6;
            {var subQ0=sQuery(id+"F1.wireOp",EDGE,"E20");var subQ1=sQuery(id+"F1.wireOp",EDGE,"E3");var subQ2=makeQuery(id+"F1.imprint","INTERSECT",VERTEX,{"derivedFrom":[subQ1,subQ0]});Q6=makeQuery(id+"F1.imprint","IMPRINT",FACE,{"disambiguationData":[TD([[makeQuery(id+"F1.imprint","IMPRINT",EDGE,{"disambiguationData":[TD([[subQ2,1.0]])],"derivedFrom":subQ1}),-1.0]])]});}
            var Q7;
            {var subQ1=sQuery(id+"F1.wireOp",EDGE,"E4");var subQ3=sQuery(id+"F1.wireOp",EDGE,"E14");var subQ4=makeQuery(id+"F1.imprint","INTERSECT",VERTEX,{"derivedFrom":[subQ1,subQ3]});Q7=makeQuery(id+"F1.imprint","IMPRINT",FACE,{"disambiguationData":[TD([[makeQuery(id+"F1.imprint","IMPRINT",EDGE,{"disambiguationData":[TD([[subQ4,1.0]])],"derivedFrom":subQ3}),1.0]])]});}
            var Q8;
            {var subQ3=sQuery(id+"F1.wireOp",EDGE,"6cIBHAnO-3Gdr-gs2R-q8mb-qejxkHO2rhEE");var subQ5=sQuery(id+"F1.wireOp",EDGE,"E14");var subQ6=makeQuery(id+"F1.imprint","INTERSECT",VERTEX,{"derivedFrom":[subQ5,subQ3]});Q8=makeQuery(id+"F1.imprint","IMPRINT",FACE,{"disambiguationData":[TD([[makeQuery(id+"F1.imprint","IMPRINT",EDGE,{"disambiguationData":[TD([[subQ6,-1.0]])],"derivedFrom":subQ5}),1.0]])]});}
            var Q9;
            {var subQ0=sQuery(id+"F1.wireOp",EDGE,"E22");var subQ1=sQuery(id+"F1.wireOp",EDGE,"E14");var subQ2=makeQuery(id+"F1.imprint","INTERSECT",VERTEX,{"derivedFrom":[subQ1,subQ0]});Q9=makeQuery(id+"F1.imprint","IMPRINT",FACE,{"disambiguationData":[TD([[makeQuery(id+"F1.imprint","IMPRINT",EDGE,{"disambiguationData":[TD([[subQ2,-1.0]])],"derivedFrom":subQ1}),1.0]])]});}
            var Q10;
            {var subQ3=sQuery(id+"F1.wireOp",EDGE,"1679b663-5bbc-411f-b373-dbe6ce103e45.trimOffspring");var subQ5=sQuery(id+"F1.wireOp",EDGE,"E14");var subQ7=makeQuery(id+"F1.imprint","INTERSECT",VERTEX,{"disambiguationData":[OD(1.0)],"derivedFrom":[subQ5,subQ3]});Q10=makeQuery(id+"F1.imprint","IMPRINT",FACE,{"disambiguationData":[TD([[makeQuery(id+"F1.imprint","IMPRINT",EDGE,{"disambiguationData":[TD([[subQ7,-1.0]])],"derivedFrom":subQ5}),1.0]])]});}
            var Q11;
            {var subQ3=sQuery(id+"F1.wireOp",EDGE,"8l5Dcz2D-qY2G-ceuh-glFK-kLwJx8DI5XpU");var subQ5=sQuery(id+"F1.wireOp",EDGE,"E14");var subQ7=makeQuery(id+"F1.imprint","INTERSECT",VERTEX,{"derivedFrom":[subQ5,subQ3]});Q11=makeQuery(id+"F1.imprint","IMPRINT",FACE,{"disambiguationData":[TD([[makeQuery(id+"F1.imprint","IMPRINT",EDGE,{"disambiguationData":[TD([[subQ7,-1.0]])],"derivedFrom":subQ5}),1.0]])]});}
            var Q12;
            {var subQ0=sQuery(id+"F1.wireOp",EDGE,"n5LII22h-w08l-qE72-yfr9-18N67uZxNTdQ");var subQ1=sQuery(id+"F1.wireOp",EDGE,"E3");var subQ2=makeQuery(id+"F1.imprint","INTERSECT",VERTEX,{"derivedFrom":[subQ1,subQ0]});Q12=makeQuery(id+"F1.imprint","IMPRINT",FACE,{"disambiguationData":[TD([[makeQuery(id+"F1.imprint","IMPRINT",EDGE,{"disambiguationData":[TD([[subQ2,-1.0]])],"derivedFrom":subQ1}),-1.0]])]});}
            var Q13;
            {var subQ0=sQuery(id+"F1.wireOp",EDGE,"KU0cdiGB-8eOj-Trs3-v5YD-3LzdnCRRimhK");var subQ1=sQuery(id+"F1.wireOp",EDGE,"E3");var subQ2=makeQuery(id+"F1.imprint","INTERSECT",VERTEX,{"derivedFrom":[subQ1,subQ0]});Q13=makeQuery(id+"F1.imprint","IMPRINT",FACE,{"disambiguationData":[TD([[makeQuery(id+"F1.imprint","IMPRINT",EDGE,{"disambiguationData":[TD([[subQ2,-1.0]])],"derivedFrom":subQ1}),-1.0]])]});}
            var Q14;
            {var subQ0=sQuery(id+"F1.wireOp",EDGE,"SVIod6WE-LFFt-Ms97-owyS-8ShU65W6W8it");var subQ1=sQuery(id+"F1.wireOp",EDGE,"E3");var subQ2=makeQuery(id+"F1.imprint","INTERSECT",VERTEX,{"derivedFrom":[subQ1,subQ0]});Q14=makeQuery(id+"F1.imprint","IMPRINT",FACE,{"disambiguationData":[TD([[makeQuery(id+"F1.imprint","IMPRINT",EDGE,{"disambiguationData":[TD([[subQ2,-1.0]])],"derivedFrom":subQ1}),-1.0]])]});}
            var Q15;
            {var subQ0=sQuery(id+"F1.wireOp",EDGE,"SVIod6WE-LFFt-Ms97-owyS-8ShU65W6W8it");var subQ1=sQuery(id+"F1.wireOp",EDGE,"E3");var subQ2=makeQuery(id+"F1.imprint","INTERSECT",VERTEX,{"derivedFrom":[subQ1,subQ0]});Q15=makeQuery(id+"F1.imprint","IMPRINT",FACE,{"disambiguationData":[TD([[makeQuery(id+"F1.imprint","IMPRINT",EDGE,{"disambiguationData":[TD([[subQ2,1.0]])],"derivedFrom":subQ1}),-1.0]])]});}
            var Q16;
            {var subQ0=sQuery(id+"F1.wireOp",EDGE,"E24");var subQ1=sQuery(id+"F1.wireOp",EDGE,"E3");var subQ2=makeQuery(id+"F1.imprint","INTERSECT",VERTEX,{"derivedFrom":[subQ1,subQ0]});Q16=makeQuery(id+"F1.imprint","IMPRINT",FACE,{"disambiguationData":[TD([[makeQuery(id+"F1.imprint","IMPRINT",EDGE,{"disambiguationData":[TD([[subQ2,-1.0]])],"derivedFrom":subQ1}),-1.0]])]});}
            var Q17;
            {var subQ0=sQuery(id+"F1.wireOp",EDGE,"E23");var subQ1=sQuery(id+"F1.wireOp",EDGE,"E3");var subQ2=makeQuery(id+"F1.imprint","INTERSECT",VERTEX,{"derivedFrom":[subQ1,subQ0]});Q17=makeQuery(id+"F1.imprint","IMPRINT",FACE,{"disambiguationData":[TD([[makeQuery(id+"F1.imprint","IMPRINT",EDGE,{"disambiguationData":[TD([[subQ2,-1.0]])],"derivedFrom":subQ1}),-1.0]])]});}
            var Q18;
            {var subQ1=sQuery(id+"F1.wireOp",EDGE,"E27");var subQ3=sQuery(id+"F1.wireOp",EDGE,"E3");var subQ4=makeQuery(id+"F1.imprint","INTERSECT",VERTEX,{"derivedFrom":[subQ3,subQ1]});Q18=makeQuery(id+"F1.imprint","IMPRINT",FACE,{"disambiguationData":[TD([[makeQuery(id+"F1.imprint","IMPRINT",EDGE,{"disambiguationData":[TD([[subQ4,-1.0]])],"derivedFrom":subQ3}),-1.0]])]});}
            var Q19;
            {var subQ0=sQuery(id+"F1.wireOp",EDGE,"E30");var subQ1=sQuery(id+"F1.wireOp",EDGE,"E3");var subQ2=makeQuery(id+"F1.imprint","INTERSECT",VERTEX,{"derivedFrom":[subQ1,subQ0]});Q19=makeQuery(id+"F1.imprint","IMPRINT",FACE,{"disambiguationData":[TD([[makeQuery(id+"F1.imprint","IMPRINT",EDGE,{"disambiguationData":[TD([[subQ2,-1.0]])],"derivedFrom":subQ1}),-1.0]])]});}
            var Q20;
            {var subQ0=sQuery(id+"F1.wireOp",EDGE,"E25");var subQ7=sQuery(id+"F1.wireOp",EDGE,"E3");var subQ8=makeQuery(id+"F1.imprint","INTERSECT",VERTEX,{"derivedFrom":[subQ7,subQ0]});Q20=makeQuery(id+"F1.imprint","IMPRINT",FACE,{"disambiguationData":[TD([[makeQuery(id+"F1.imprint","IMPRINT",EDGE,{"disambiguationData":[TD([[subQ8,-1.0]])],"derivedFrom":subQ7}),-1.0]])]});}
            extrude(context, id + "F5", {"entities" : qUnion([Q0, Q1, Q2, Q3, Q4, Q5, Q6, Q7, Q8, Q9, Q10, Q11, Q12, Q13, Q14, Q15, Q16, Q17, Q18, Q19, Q20]), "operationType" : NewBodyOperationType.ADD, "depth" : 50.8 * mm});
        }
        {
            var Q0;
            {var subQ5=sQuery(id+"F1.wireOp",EDGE,"E12");Q0=makeQuery(id+"F1.imprint","IMPRINT",FACE,{"disambiguationData":[TD([[makeQuery(id+"F1.imprint","IMPRINT",EDGE,{"derivedFrom":subQ5}),-1.0]])]});}
            var Q1;
            {var subQ0=sQuery(id+"F1.wireOp",EDGE,"E13");Q1=makeQuery(id+"F1.imprint","IMPRINT",FACE,{"disambiguationData":[TD([[makeQuery(id+"F1.imprint","IMPRINT",EDGE,{"derivedFrom":subQ0}),1.0]])]});}
            var Q2;
            {var subQ0=sQuery(id+"F1.wireOp",EDGE,"E4");var subQ1=sQuery(id+"F1.wireOp",EDGE,"E3");var subQ2=makeQuery(id+"F1.imprint","INTERSECT",VERTEX,{"derivedFrom":[subQ1,subQ0]});Q2=makeQuery(id+"F1.imprint","IMPRINT",FACE,{"disambiguationData":[TD([[makeQuery(id+"F1.imprint","IMPRINT",EDGE,{"disambiguationData":[TD([[subQ2,-1.0]])],"derivedFrom":subQ1}),-1.0]])]});}
            var Q3;
            {var subQ2=sQuery(id+"F1.wireOp",EDGE,"E12");Q3=makeQuery(id+"F1.imprint","IMPRINT",FACE,{"disambiguationData":[TD([[makeQuery(id+"F1.imprint","IMPRINT",EDGE,{"derivedFrom":subQ2}),1.0]])]});}
            var Q4;
            {var subQ0=sQuery(id+"F1.wireOp",EDGE,"E17");Q4=makeQuery(id+"F1.imprint","IMPRINT",FACE,{"disambiguationData":[TD([[makeQuery(id+"F1.imprint","IMPRINT",EDGE,{"derivedFrom":subQ0}),-1.0]])]});}
            var Q5;
            {var subQ0=sQuery(id+"F1.wireOp",EDGE,"E6");var subQ5=sQuery(id+"F1.wireOp",EDGE,"E14");var subQ6=makeQuery(id+"F1.imprint","INTERSECT",VERTEX,{"derivedFrom":[subQ0,subQ5]});Q5=makeQuery(id+"F1.imprint","IMPRINT",FACE,{"disambiguationData":[TD([[makeQuery(id+"F1.imprint","IMPRINT",EDGE,{"disambiguationData":[TD([[subQ6,1.0]])],"derivedFrom":subQ5}),1.0]])]});}
            var Q6;
            {var subQ0=sQuery(id+"F1.wireOp",EDGE,"E16.trimOffspring");Q6=makeQuery(id+"F1.imprint","IMPRINT",FACE,{"disambiguationData":[TD([[makeQuery(id+"F1.imprint","IMPRINT",EDGE,{"derivedFrom":subQ0}),1.0]])]});}
            var Q7;
            {var subQ2=sQuery(id+"F1.wireOp",EDGE,"E15.trimOffspring");Q7=makeQuery(id+"F1.imprint","IMPRINT",FACE,{"disambiguationData":[TD([[makeQuery(id+"F1.imprint","IMPRINT",EDGE,{"derivedFrom":subQ2}),1.0]])]});}
            var Q8;
            {var subQ5=sQuery(id+"F1.wireOp",EDGE,"E15.trimOffspring");Q8=makeQuery(id+"F1.imprint","IMPRINT",FACE,{"disambiguationData":[TD([[makeQuery(id+"F1.imprint","IMPRINT",EDGE,{"derivedFrom":subQ5}),-1.0]])]});}
            var Q9;
            {var subQ0=sQuery(id+"F1.wireOp",EDGE,"8l5Dcz2D-qY2G-ceuh-glFK-kLwJx8DI5XpU");var subQ3=sQuery(id+"F1.wireOp",EDGE,"E18");var subQ5=makeQuery(id+"F1.imprint","INTERSECT",VERTEX,{"derivedFrom":[subQ3,subQ0]});Q9=makeQuery(id+"F1.imprint","IMPRINT",FACE,{"disambiguationData":[TD([[makeQuery(id+"F1.imprint","IMPRINT",EDGE,{"disambiguationData":[TD([[subQ5,-1.0]])],"derivedFrom":subQ3}),-1.0]])]});}
            var Q10;
            {var subQ1=sQuery(id+"F1.wireOp",EDGE,"E21");var subQ5=sQuery(id+"F1.wireOp",EDGE,"E18");var subQ6=makeQuery(id+"F1.imprint","INTERSECT",VERTEX,{"derivedFrom":[subQ5,subQ1]});Q10=makeQuery(id+"F1.imprint","IMPRINT",FACE,{"disambiguationData":[TD([[makeQuery(id+"F1.imprint","IMPRINT",EDGE,{"disambiguationData":[TD([[subQ6,-1.0]])],"derivedFrom":subQ5}),-1.0]])]});}
            var Q11;
            {var subQ1=sQuery(id+"F1.wireOp",EDGE,"E19");var subQ7=sQuery(id+"F1.wireOp",EDGE,"E17");var subQ8=makeQuery(id+"F1.imprint","INTERSECT",VERTEX,{"derivedFrom":[subQ7,subQ1]});Q11=makeQuery(id+"F1.imprint","IMPRINT",FACE,{"disambiguationData":[TD([[makeQuery(id+"F1.imprint","IMPRINT",EDGE,{"disambiguationData":[TD([[subQ8,-1.0]])],"derivedFrom":subQ7}),-1.0]])]});}
            var Q12;
            {var subQ3=sQuery(id+"F1.wireOp",EDGE,"E17");var subQ9=sQuery(id+"F1.wireOp",EDGE,"E22");var subQ10=makeQuery(id+"F1.imprint","INTERSECT",VERTEX,{"derivedFrom":[subQ3,subQ9]});Q12=makeQuery(id+"F1.imprint","IMPRINT",FACE,{"disambiguationData":[TD([[makeQuery(id+"F1.imprint","IMPRINT",EDGE,{"disambiguationData":[TD([[subQ10,-1.0]])],"derivedFrom":subQ3}),-1.0]])]});}
            var Q13;
            {var subQ0=sQuery(id+"F1.wireOp",EDGE,"E22");var subQ1=sQuery(id+"F1.wireOp",EDGE,"E17");var subQ2=makeQuery(id+"F1.imprint","INTERSECT",VERTEX,{"derivedFrom":[subQ1,subQ0]});Q13=makeQuery(id+"F1.imprint","IMPRINT",FACE,{"disambiguationData":[TD([[makeQuery(id+"F1.imprint","IMPRINT",EDGE,{"disambiguationData":[TD([[subQ2,1.0]])],"derivedFrom":subQ0}),1.0]])]});}
            var Q14;
            {var subQ3=sQuery(id+"F1.wireOp",EDGE,"E17");var subQ11=sQuery(id+"F1.wireOp",EDGE,"E23");var subQ12=makeQuery(id+"F1.imprint","INTERSECT",VERTEX,{"derivedFrom":[subQ3,subQ11]});Q14=makeQuery(id+"F1.imprint","IMPRINT",FACE,{"disambiguationData":[TD([[makeQuery(id+"F1.imprint","IMPRINT",EDGE,{"disambiguationData":[TD([[subQ12,-1.0]])],"derivedFrom":subQ3}),-1.0]])]});}
            var Q15;
            {var subQ0=sQuery(id+"F1.wireOp",EDGE,"E20");var subQ1=sQuery(id+"F1.wireOp",EDGE,"E18");var subQ2=makeQuery(id+"F1.imprint","INTERSECT",VERTEX,{"derivedFrom":[subQ1,subQ0]});Q15=makeQuery(id+"F1.imprint","IMPRINT",FACE,{"disambiguationData":[TD([[makeQuery(id+"F1.imprint","IMPRINT",EDGE,{"disambiguationData":[TD([[subQ2,1.0]])],"derivedFrom":subQ0}),1.0]])]});}
            var Q16;
            {var subQ0=sQuery(id+"F1.wireOp",EDGE,"E18");var subQ3=sQuery(id+"F1.wireOp",EDGE,"E23");var subQ4=makeQuery(id+"F1.imprint","INTERSECT",VERTEX,{"derivedFrom":[subQ0,subQ3]});Q16=makeQuery(id+"F1.imprint","IMPRINT",FACE,{"disambiguationData":[TD([[makeQuery(id+"F1.imprint","IMPRINT",EDGE,{"disambiguationData":[TD([[subQ4,1.0]])],"derivedFrom":subQ3}),-1.0]])]});}
            var Q17;
            {var subQ0=sQuery(id+"F1.wireOp",EDGE,"E24");var subQ3=sQuery(id+"F1.wireOp",EDGE,"E25");var subQ4=makeQuery(id+"F1.imprint","INTERSECT",VERTEX,{"derivedFrom":[subQ0,subQ3]});Q17=makeQuery(id+"F1.imprint","IMPRINT",FACE,{"disambiguationData":[TD([[makeQuery(id+"F1.imprint","IMPRINT",EDGE,{"disambiguationData":[TD([[subQ4,1.0]])],"derivedFrom":subQ0}),1.0]])]});}
            var Q18;
            {var subQ0=sQuery(id+"F1.wireOp",EDGE,"E20");var subQ1=sQuery(id+"F1.wireOp",EDGE,"E19");var subQ2=makeQuery(id+"F1.imprint","INTERSECT",VERTEX,{"derivedFrom":[subQ1,subQ0]});Q18=makeQuery(id+"F1.imprint","IMPRINT",FACE,{"disambiguationData":[TD([[makeQuery(id+"F1.imprint","IMPRINT",EDGE,{"disambiguationData":[TD([[subQ2,-1.0]])],"derivedFrom":subQ1}),-1.0]])]});}
            var Q19;
            {var subQ0=sQuery(id+"F1.wireOp",EDGE,"E22");var subQ1=sQuery(id+"F1.wireOp",EDGE,"E21");var subQ2=makeQuery(id+"F1.imprint","INTERSECT",VERTEX,{"derivedFrom":[subQ1,subQ0]});Q19=makeQuery(id+"F1.imprint","IMPRINT",FACE,{"disambiguationData":[TD([[makeQuery(id+"F1.imprint","IMPRINT",EDGE,{"disambiguationData":[TD([[subQ2,-1.0]])],"derivedFrom":subQ1}),-1.0]])]});}
            var Q20;
            {var subQ0=sQuery(id+"F1.wireOp",EDGE,"E25");var subQ1=sQuery(id+"F1.wireOp",EDGE,"E17");var subQ2=makeQuery(id+"F1.imprint","INTERSECT",VERTEX,{"derivedFrom":[subQ1,subQ0]});Q20=makeQuery(id+"F1.imprint","IMPRINT",FACE,{"disambiguationData":[TD([[makeQuery(id+"F1.imprint","IMPRINT",EDGE,{"disambiguationData":[TD([[subQ2,-1.0]])],"derivedFrom":subQ1}),-1.0]])]});}
            var Q21;
            {var subQ0=sQuery(id+"F1.wireOp",EDGE,"E26");var subQ1=sQuery(id+"F1.wireOp",EDGE,"E18");var subQ2=makeQuery(id+"F1.imprint","INTERSECT",VERTEX,{"derivedFrom":[subQ1,subQ0]});Q21=makeQuery(id+"F1.imprint","IMPRINT",FACE,{"disambiguationData":[TD([[makeQuery(id+"F1.imprint","IMPRINT",EDGE,{"disambiguationData":[TD([[subQ2,-1.0]])],"derivedFrom":subQ1}),-1.0]])]});}
            var Q22;
            {var subQ0=sQuery(id+"F1.wireOp",EDGE,"E20");var subQ1=sQuery(id+"F1.wireOp",EDGE,"E18");var subQ2=makeQuery(id+"F1.imprint","INTERSECT",VERTEX,{"derivedFrom":[subQ1,subQ0]});Q22=makeQuery(id+"F1.imprint","IMPRINT",FACE,{"disambiguationData":[TD([[makeQuery(id+"F1.imprint","IMPRINT",EDGE,{"disambiguationData":[TD([[subQ2,-1.0]])],"derivedFrom":subQ1}),-1.0]])]});}
            extrude(context, id + "F6", {"entities" : qUnion([Q0, Q1, Q2, Q3, Q4, Q5, Q6, Q7, Q8, Q9, Q10, Q11, Q12, Q13, Q14, Q15, Q16, Q17, Q18, Q19, Q20, Q21, Q22]), "operationType" : NewBodyOperationType.ADD, "depth" : 50.8 * mm});
        }
        {
            var Q0;
            {var subQ0=sQuery(id+"F1.wireOp",EDGE,"SVIod6WE-LFFt-Ms97-owyS-8ShU65W6W8it");var subQ1=sQuery(id+"F1.wireOp",EDGE,"E3");var subQ2=makeQuery(id+"F1.imprint","INTERSECT",VERTEX,{"derivedFrom":[subQ1,subQ0]});Q0=makeQuery(id+"F1.imprint","IMPRINT",FACE,{"disambiguationData":[TD([[makeQuery(id+"F1.imprint","IMPRINT",EDGE,{"disambiguationData":[TD([[subQ2,1.0]])],"derivedFrom":subQ1}),1.0]])]});}
            var Q1;
            {var subQ1=sQuery(id+"F1.wireOp",EDGE,"E3");var subQ3=sQuery(id+"F1.wireOp",EDGE,"I2xWRYXB-6D2N-iSpQ-MyaY-Cu2MAQN8JGNk");var subQ4=makeQuery(id+"F1.imprint","INTERSECT",VERTEX,{"derivedFrom":[subQ1,subQ3]});Q1=makeQuery(id+"F1.imprint","IMPRINT",FACE,{"disambiguationData":[TD([[makeQuery(id+"F1.imprint","IMPRINT",EDGE,{"disambiguationData":[TD([[subQ4,-1.0]])],"derivedFrom":subQ1}),1.0]])]});}
            var Q2;
            {var subQ0=sQuery(id+"F1.wireOp",EDGE,"n5LII22h-w08l-qE72-yfr9-18N67uZxNTdQ");var subQ1=sQuery(id+"F1.wireOp",EDGE,"E3");var subQ2=makeQuery(id+"F1.imprint","INTERSECT",VERTEX,{"derivedFrom":[subQ1,subQ0]});Q2=makeQuery(id+"F1.imprint","IMPRINT",FACE,{"disambiguationData":[TD([[makeQuery(id+"F1.imprint","IMPRINT",EDGE,{"disambiguationData":[TD([[subQ2,-1.0]])],"derivedFrom":subQ1}),1.0]])]});}
            var Q3;
            {var subQ0=sQuery(id+"F1.wireOp",EDGE,"E22");var subQ1=sQuery(id+"F1.wireOp",EDGE,"E3");var subQ2=makeQuery(id+"F1.imprint","INTERSECT",VERTEX,{"derivedFrom":[subQ1,subQ0]});Q3=makeQuery(id+"F1.imprint","IMPRINT",FACE,{"disambiguationData":[TD([[makeQuery(id+"F1.imprint","IMPRINT",EDGE,{"disambiguationData":[TD([[subQ2,-1.0]])],"derivedFrom":subQ1}),1.0]])]});}
            var Q4;
            {var subQ0=sQuery(id+"F1.wireOp",EDGE,"E27");var subQ1=sQuery(id+"F1.wireOp",EDGE,"E3");var subQ2=makeQuery(id+"F1.imprint","INTERSECT",VERTEX,{"derivedFrom":[subQ1,subQ0]});Q4=makeQuery(id+"F1.imprint","IMPRINT",FACE,{"disambiguationData":[TD([[makeQuery(id+"F1.imprint","IMPRINT",EDGE,{"disambiguationData":[TD([[subQ2,-1.0]])],"derivedFrom":subQ1}),1.0]])]});}
            var Q5;
            {var subQ0=sQuery(id+"F1.wireOp",EDGE,"E19");var subQ1=sQuery(id+"F1.wireOp",EDGE,"E0");var subQ2=makeQuery(id+"F1.imprint","INTERSECT",VERTEX,{"derivedFrom":[subQ1,subQ0]});Q5=makeQuery(id+"F1.imprint","IMPRINT",FACE,{"disambiguationData":[TD([[makeQuery(id+"F1.imprint","IMPRINT",EDGE,{"disambiguationData":[TD([[subQ2,-1.0]])],"derivedFrom":subQ1}),1.0]])]});}
            var Q6;
            {var subQ0=sQuery(id+"F1.wireOp",EDGE,"E19");var subQ1=sQuery(id+"F1.wireOp",EDGE,"E10.trimOffspring");var subQ2=makeQuery(id+"F1.imprint","INTERSECT",VERTEX,{"derivedFrom":[subQ1,subQ0]});Q6=makeQuery(id+"F1.imprint","IMPRINT",FACE,{"disambiguationData":[TD([[makeQuery(id+"F1.imprint","IMPRINT",EDGE,{"disambiguationData":[TD([[subQ2,-1.0]])],"derivedFrom":subQ1}),-1.0]])]});}
            var Q7;
            {var subQ0=sQuery(id+"F1.wireOp",EDGE,"E19");var subQ1=sQuery(id+"F1.wireOp",EDGE,"E10.trimOffspring");var subQ2=makeQuery(id+"F1.imprint","INTERSECT",VERTEX,{"derivedFrom":[subQ1,subQ0]});Q7=makeQuery(id+"F1.imprint","IMPRINT",FACE,{"disambiguationData":[TD([[makeQuery(id+"F1.imprint","IMPRINT",EDGE,{"disambiguationData":[TD([[subQ2,-1.0]])],"derivedFrom":subQ1}),1.0]])]});}
            var Q8;
            {var subQ0=sQuery(id+"F1.wireOp",EDGE,"E19");var subQ1=sQuery(id+"F1.wireOp",EDGE,"E3");var subQ2=makeQuery(id+"F1.imprint","INTERSECT",VERTEX,{"derivedFrom":[subQ1,subQ0]});Q8=makeQuery(id+"F1.imprint","IMPRINT",FACE,{"disambiguationData":[TD([[makeQuery(id+"F1.imprint","IMPRINT",EDGE,{"disambiguationData":[TD([[subQ2,-1.0]])],"derivedFrom":subQ1}),-1.0]])]});}
            var Q9;
            {var subQ1=sQuery(id+"F1.wireOp",EDGE,"E19");var subQ6=sQuery(id+"F1.wireOp",EDGE,"E3");var subQ9=makeQuery(id+"F1.imprint","INTERSECT",VERTEX,{"derivedFrom":[subQ6,subQ1]});Q9=makeQuery(id+"F1.imprint","IMPRINT",FACE,{"disambiguationData":[TD([[makeQuery(id+"F1.imprint","IMPRINT",EDGE,{"disambiguationData":[TD([[subQ9,-1.0]])],"derivedFrom":subQ6}),1.0]])]});}
            var Q10;
            {var subQ0=sQuery(id+"F1.wireOp",EDGE,"E22");var subQ1=sQuery(id+"F1.wireOp",EDGE,"E17");var subQ2=makeQuery(id+"F1.imprint","INTERSECT",VERTEX,{"derivedFrom":[subQ1,subQ0]});Q10=makeQuery(id+"F1.imprint","IMPRINT",FACE,{"disambiguationData":[TD([[makeQuery(id+"F1.imprint","IMPRINT",EDGE,{"disambiguationData":[TD([[subQ2,-1.0]])],"derivedFrom":subQ1}),-1.0]])]});}
            var Q11;
            {var subQ1=sQuery(id+"F1.wireOp",EDGE,"E3");var subQ7=sQuery(id+"F1.wireOp",EDGE,"E20");var subQ9=makeQuery(id+"F1.imprint","INTERSECT",VERTEX,{"derivedFrom":[subQ1,subQ7]});Q11=makeQuery(id+"F1.imprint","IMPRINT",FACE,{"disambiguationData":[TD([[makeQuery(id+"F1.imprint","IMPRINT",EDGE,{"disambiguationData":[TD([[subQ9,1.0]])],"derivedFrom":subQ1}),1.0]])]});}
            var Q12;
            {var subQ0=sQuery(id+"F1.wireOp",EDGE,"E20");var subQ1=sQuery(id+"F1.wireOp",EDGE,"E3");var subQ2=makeQuery(id+"F1.imprint","INTERSECT",VERTEX,{"derivedFrom":[subQ1,subQ0]});Q12=makeQuery(id+"F1.imprint","IMPRINT",FACE,{"disambiguationData":[TD([[makeQuery(id+"F1.imprint","IMPRINT",EDGE,{"disambiguationData":[TD([[subQ2,1.0]])],"derivedFrom":subQ1}),-1.0]])]});}
            var Q13;
            {var subQ0=sQuery(id+"F1.wireOp",EDGE,"E21");var subQ1=sQuery(id+"F1.wireOp",EDGE,"E2");var subQ2=makeQuery(id+"F1.imprint","INTERSECT",VERTEX,{"derivedFrom":[subQ1,subQ0]});Q13=makeQuery(id+"F1.imprint","IMPRINT",FACE,{"disambiguationData":[TD([[makeQuery(id+"F1.imprint","IMPRINT",EDGE,{"disambiguationData":[TD([[subQ2,-1.0]])],"derivedFrom":subQ1}),1.0]])]});}
            var Q14;
            {var subQ0=sQuery(id+"F1.wireOp",EDGE,"E20");var subQ1=sQuery(id+"F1.wireOp",EDGE,"E0");var subQ2=makeQuery(id+"F1.imprint","INTERSECT",VERTEX,{"derivedFrom":[subQ1,subQ0]});Q14=makeQuery(id+"F1.imprint","IMPRINT",FACE,{"disambiguationData":[TD([[makeQuery(id+"F1.imprint","IMPRINT",EDGE,{"disambiguationData":[TD([[subQ2,1.0]])],"derivedFrom":subQ1}),1.0]])]});}
            var Q15;
            {var subQ0=sQuery(id+"F1.wireOp",EDGE,"E22");var subQ1=sQuery(id+"F1.wireOp",EDGE,"E17");var subQ2=makeQuery(id+"F1.imprint","INTERSECT",VERTEX,{"derivedFrom":[subQ1,subQ0]});Q15=makeQuery(id+"F1.imprint","IMPRINT",FACE,{"disambiguationData":[TD([[makeQuery(id+"F1.imprint","IMPRINT",EDGE,{"disambiguationData":[TD([[subQ2,-1.0]])],"derivedFrom":subQ1}),1.0]])]});}
            var Q16;
            {var subQ0=sQuery(id+"F1.wireOp",EDGE,"E20");var subQ1=sQuery(id+"F1.wireOp",EDGE,"E18");var subQ2=makeQuery(id+"F1.imprint","INTERSECT",VERTEX,{"derivedFrom":[subQ1,subQ0]});Q16=makeQuery(id+"F1.imprint","IMPRINT",FACE,{"disambiguationData":[TD([[makeQuery(id+"F1.imprint","IMPRINT",EDGE,{"disambiguationData":[TD([[subQ2,-1.0]])],"derivedFrom":subQ1}),1.0]])]});}
            var Q17;
            {var subQ0=sQuery(id+"F1.wireOp",EDGE,"E23");var subQ1=sQuery(id+"F1.wireOp",EDGE,"E17");var subQ2=makeQuery(id+"F1.imprint","INTERSECT",VERTEX,{"derivedFrom":[subQ1,subQ0]});Q17=makeQuery(id+"F1.imprint","IMPRINT",FACE,{"disambiguationData":[TD([[makeQuery(id+"F1.imprint","IMPRINT",EDGE,{"disambiguationData":[TD([[subQ2,-1.0]])],"derivedFrom":subQ1}),1.0]])]});}
            var Q18;
            {var subQ0=sQuery(id+"F1.wireOp",EDGE,"E24");var subQ1=sQuery(id+"F1.wireOp",EDGE,"E18");var subQ2=makeQuery(id+"F1.imprint","INTERSECT",VERTEX,{"derivedFrom":[subQ1,subQ0]});Q18=makeQuery(id+"F1.imprint","IMPRINT",FACE,{"disambiguationData":[TD([[makeQuery(id+"F1.imprint","IMPRINT",EDGE,{"disambiguationData":[TD([[subQ2,-1.0]])],"derivedFrom":subQ1}),1.0]])]});}
            var Q19;
            {var subQ0=sQuery(id+"F1.wireOp",EDGE,"KU0cdiGB-8eOj-Trs3-v5YD-3LzdnCRRimhK");var subQ3=sQuery(id+"F1.wireOp",EDGE,"E3");var subQ4=makeQuery(id+"F1.imprint","INTERSECT",VERTEX,{"derivedFrom":[subQ3,subQ0]});Q19=makeQuery(id+"F1.imprint","IMPRINT",FACE,{"disambiguationData":[TD([[makeQuery(id+"F1.imprint","IMPRINT",EDGE,{"disambiguationData":[TD([[subQ4,-1.0]])],"derivedFrom":subQ3}),1.0]])]});}
            var Q20;
            {var subQ0=sQuery(id+"F1.wireOp",EDGE,"E25");var subQ1=sQuery(id+"F1.wireOp",EDGE,"E17");var subQ2=makeQuery(id+"F1.imprint","INTERSECT",VERTEX,{"derivedFrom":[subQ1,subQ0]});Q20=makeQuery(id+"F1.imprint","IMPRINT",FACE,{"disambiguationData":[TD([[makeQuery(id+"F1.imprint","IMPRINT",EDGE,{"disambiguationData":[TD([[subQ2,-1.0]])],"derivedFrom":subQ1}),1.0]])]});}
            var Q21;
            {var subQ0=sQuery(id+"F1.wireOp",EDGE,"E26");var subQ1=sQuery(id+"F1.wireOp",EDGE,"E18");var subQ2=makeQuery(id+"F1.imprint","INTERSECT",VERTEX,{"derivedFrom":[subQ1,subQ0]});Q21=makeQuery(id+"F1.imprint","IMPRINT",FACE,{"disambiguationData":[TD([[makeQuery(id+"F1.imprint","IMPRINT",EDGE,{"disambiguationData":[TD([[subQ2,-1.0]])],"derivedFrom":subQ1}),1.0]])]});}
            var Q22;
            {var subQ3=sQuery(id+"F1.wireOp",EDGE,"E25");var subQ5=sQuery(id+"F1.wireOp",EDGE,"E3");var subQ6=makeQuery(id+"F1.imprint","INTERSECT",VERTEX,{"derivedFrom":[subQ5,subQ3]});Q22=makeQuery(id+"F1.imprint","IMPRINT",FACE,{"disambiguationData":[TD([[makeQuery(id+"F1.imprint","IMPRINT",EDGE,{"disambiguationData":[TD([[subQ6,-1.0]])],"derivedFrom":subQ5}),1.0]])]});}
            var Q23;
            {var subQ0=sQuery(id+"F1.wireOp",EDGE,"E27");var subQ1=sQuery(id+"F1.wireOp",EDGE,"E3");var subQ2=makeQuery(id+"F1.imprint","INTERSECT",VERTEX,{"derivedFrom":[subQ1,subQ0]});Q23=makeQuery(id+"F1.imprint","IMPRINT",FACE,{"disambiguationData":[TD([[makeQuery(id+"F1.imprint","IMPRINT",EDGE,{"disambiguationData":[TD([[subQ2,-1.0]])],"derivedFrom":subQ1}),1.0]])]});}
            var Q24;
            {var subQ0=sQuery(id+"F1.wireOp",EDGE,"SVIod6WE-LFFt-Ms97-owyS-8ShU65W6W8it");var subQ7=sQuery(id+"F1.wireOp",EDGE,"E3");var subQ9=makeQuery(id+"F1.imprint","INTERSECT",VERTEX,{"derivedFrom":[subQ7,subQ0]});Q24=makeQuery(id+"F1.imprint","IMPRINT",FACE,{"disambiguationData":[TD([[makeQuery(id+"F1.imprint","IMPRINT",EDGE,{"disambiguationData":[TD([[subQ9,-1.0]])],"derivedFrom":subQ7}),1.0]])]});}
            var Q25;
            {var subQ0=sQuery(id+"F1.wireOp",EDGE,"E24");var subQ1=sQuery(id+"F1.wireOp",EDGE,"E3");var subQ2=makeQuery(id+"F1.imprint","INTERSECT",VERTEX,{"derivedFrom":[subQ1,subQ0]});Q25=makeQuery(id+"F1.imprint","IMPRINT",FACE,{"disambiguationData":[TD([[makeQuery(id+"F1.imprint","IMPRINT",EDGE,{"disambiguationData":[TD([[subQ2,-1.0]])],"derivedFrom":subQ1}),1.0]])]});}
            var Q26;
            {var subQ0=sQuery(id+"F1.wireOp",EDGE,"E23");var subQ1=sQuery(id+"F1.wireOp",EDGE,"E3");var subQ2=makeQuery(id+"F1.imprint","INTERSECT",VERTEX,{"derivedFrom":[subQ1,subQ0]});Q26=makeQuery(id+"F1.imprint","IMPRINT",FACE,{"disambiguationData":[TD([[makeQuery(id+"F1.imprint","IMPRINT",EDGE,{"disambiguationData":[TD([[subQ2,-1.0]])],"derivedFrom":subQ1}),1.0]])]});}
            var Q27;
            {var subQ1=sQuery(id+"F1.wireOp",EDGE,"E3");var subQ3=sQuery(id+"F1.wireOp",EDGE,"E23");var subQ4=makeQuery(id+"F1.imprint","INTERSECT",VERTEX,{"derivedFrom":[subQ1,subQ3]});Q27=makeQuery(id+"F1.imprint","IMPRINT",FACE,{"disambiguationData":[TD([[makeQuery(id+"F1.imprint","IMPRINT",EDGE,{"disambiguationData":[TD([[subQ4,1.0]])],"derivedFrom":subQ3}),-1.0]])]});}
            var Q28;
            {var subQ1=sQuery(id+"F1.wireOp",EDGE,"E3");var subQ3=sQuery(id+"F1.wireOp",EDGE,"E26");var subQ4=makeQuery(id+"F1.imprint","INTERSECT",VERTEX,{"derivedFrom":[subQ1,subQ3]});Q28=makeQuery(id+"F1.imprint","IMPRINT",FACE,{"disambiguationData":[TD([[makeQuery(id+"F1.imprint","IMPRINT",EDGE,{"disambiguationData":[TD([[subQ4,1.0]])],"derivedFrom":subQ3}),1.0]])]});}
            var Q29;
            {var subQ1=sQuery(id+"F1.wireOp",EDGE,"E3");var subQ3=sQuery(id+"F1.wireOp",EDGE,"KU0cdiGB-8eOj-Trs3-v5YD-3LzdnCRRimhK");var subQ4=makeQuery(id+"F1.imprint","INTERSECT",VERTEX,{"derivedFrom":[subQ1,subQ3]});Q29=makeQuery(id+"F1.imprint","IMPRINT",FACE,{"disambiguationData":[TD([[makeQuery(id+"F1.imprint","IMPRINT",EDGE,{"disambiguationData":[TD([[subQ4,1.0]])],"derivedFrom":subQ1}),1.0]])]});}
            var Q30;
            {var subQ0=sQuery(id+"F1.wireOp",EDGE,"E27");var subQ1=sQuery(id+"F1.wireOp",EDGE,"E17");var subQ2=makeQuery(id+"F1.imprint","INTERSECT",VERTEX,{"derivedFrom":[subQ1,subQ0]});Q30=makeQuery(id+"F1.imprint","IMPRINT",FACE,{"disambiguationData":[TD([[makeQuery(id+"F1.imprint","IMPRINT",EDGE,{"disambiguationData":[TD([[subQ2,-1.0]])],"derivedFrom":subQ1}),1.0]])]});}
            var Q31;
            {var subQ5=sQuery(id+"F1.wireOp",EDGE,"E36");var subQ7=sQuery(id+"F1.wireOp",EDGE,"E3");var subQ9=makeQuery(id+"F1.imprint","INTERSECT",VERTEX,{"derivedFrom":[subQ7,subQ5]});Q31=makeQuery(id+"F1.imprint","IMPRINT",FACE,{"disambiguationData":[TD([[makeQuery(id+"F1.imprint","IMPRINT",EDGE,{"disambiguationData":[TD([[subQ9,-1.0]])],"derivedFrom":subQ7}),1.0]])]});}
            var Q32;
            {var subQ5=sQuery(id+"F1.wireOp",EDGE,"E35");var subQ7=sQuery(id+"F1.wireOp",EDGE,"E3");var subQ8=makeQuery(id+"F1.imprint","INTERSECT",VERTEX,{"derivedFrom":[subQ7,subQ5]});Q32=makeQuery(id+"F1.imprint","IMPRINT",FACE,{"disambiguationData":[TD([[makeQuery(id+"F1.imprint","IMPRINT",EDGE,{"disambiguationData":[TD([[subQ8,1.0]])],"derivedFrom":subQ7}),1.0]])]});}
            var Q33;
            {var subQ5=sQuery(id+"F1.wireOp",EDGE,"E32");var subQ7=sQuery(id+"F1.wireOp",EDGE,"E3");var subQ8=makeQuery(id+"F1.imprint","INTERSECT",VERTEX,{"derivedFrom":[subQ7,subQ5]});Q33=makeQuery(id+"F1.imprint","IMPRINT",FACE,{"disambiguationData":[TD([[makeQuery(id+"F1.imprint","IMPRINT",EDGE,{"disambiguationData":[TD([[subQ8,-1.0]])],"derivedFrom":subQ7}),1.0]])]});}
            var Q34;
            {var subQ0=sQuery(id+"F1.wireOp",EDGE,"18cd6810-feed-407b-96fd-876ede30ebc9.trimOffspring");Q34=makeQuery(id+"F1.imprint","IMPRINT",FACE,{"disambiguationData":[TD([[makeQuery(id+"F1.imprint","IMPRINT",EDGE,{"derivedFrom":subQ0}),1.0]])]});}
            var Q35;
            {var subQ0=sQuery(id+"F1.wireOp",EDGE,"E21");var subQ1=sQuery(id+"F1.wireOp",EDGE,"E2");var subQ2=makeQuery(id+"F1.imprint","INTERSECT",VERTEX,{"derivedFrom":[subQ1,subQ0]});Q35=makeQuery(id+"F1.imprint","IMPRINT",FACE,{"disambiguationData":[TD([[makeQuery(id+"F1.imprint","IMPRINT",EDGE,{"disambiguationData":[TD([[subQ2,-1.0]])],"derivedFrom":subQ1}),-1.0]])]});}
            extrude(context, id + "F7", {"entities" : qUnion([Q0, Q1, Q2, Q3, Q4, Q5, Q6, Q7, Q8, Q9, Q10, Q11, Q12, Q13, Q14, Q15, Q16, Q17, Q18, Q19, Q20, Q21, Q22, Q23, Q24, Q25, Q26, Q27, Q28, Q29, Q30, Q31, Q32, Q33, Q34, Q35]), "operationType" : NewBodyOperationType.ADD, "depth" : 50.8 * mm});
        }
        {
            var Q0;
            {var subQ0=sQuery(id+"F1.wireOp",EDGE,"E20");var subQ1=sQuery(id+"F1.wireOp",EDGE,"E19");var subQ2=sQuery(id+"F1.wireOp",EDGE,"E18");var subQ3=sQuery(id+"F1.wireOp",EDGE,"E17");var subQ4=sQuery(id+"F1.wireOp",EDGE,"E7");var subQ5=sQuery(id+"F1.wireOp",EDGE,"E6");var subQ6=sQuery(id+"F1.wireOp",EDGE,"E0");var subQ7=sQuery(id+"F1.wireOp",EDGE,"E14");var subQ8=sQuery(id+"F1.wireOp",EDGE,"E15.trimOffspring");var subQ9=sQuery(id+"F1.wireOp",EDGE,"E12");var subQ10=sQuery(id+"F1.wireOp",EDGE,"E11.trimOffspring");var subQ11=sQuery(id+"F1.wireOp",EDGE,"E1");var subQ12=sQuery(id+"F1.wireOp",EDGE,"E16.trimOffspring");var subQ13=sQuery(id+"F1.wireOp",EDGE,"E13");var subQ14=sQuery(id+"F1.wireOp",EDGE,"E10.trimOffspring");var subQ15=sQuery(id+"F1.wireOp",EDGE,"E2");var subQ16=sQuery(id+"F1.wireOp",EDGE,"E4");var subQ17=sQuery(id+"F1.wireOp",EDGE,"E5");var subQ18=sQuery(id+"F1.wireOp",EDGE,"E22");var subQ19=sQuery(id+"F1.wireOp",EDGE,"E21");Q0=makeQuery(id+"F7.boolean.opBoolean","SPLIT",FACE,{"disambiguationData":[TD([makeQuery(id+"F2.opExtrude","SWEPT_FACE",FACE,{"disambiguationData":[OSD([subQ6])]}),makeQuery(id+"F2.opExtrude","CAP_FACE",FACE,{"disambiguationData":[OSD([subQ6,subQ11,subQ10,subQ9,subQ8])],"isStart":false}),makeQuery(id+"F3.opExtrude","CAP_FACE",FACE,{"disambiguationData":[OSD([subQ11,subQ15,subQ14,subQ10,subQ9,subQ13,subQ8,subQ12])],"isStart":false}),makeQuery(id+"F3.opExtrude","SWEPT_FACE",FACE,{"disambiguationData":[OSD([subQ11,subQ10,subQ9,subQ8])]}),makeQuery(id+"F4.opExtrude","CAP_FACE",FACE,{"disambiguationData":[OSD([subQ15,subQ14,subQ13,subQ7,subQ12])],"isStart":false}),makeQuery(id+"F4.opExtrude","SWEPT_FACE",FACE,{"disambiguationData":[OSD([subQ15,subQ14,subQ13,subQ12])]}),makeQuery(id+"F5.opExtrude","CAP_FACE",FACE,{"disambiguationData":[OSD([sQuery(id+"F1.wireOp",EDGE,"E3"),subQ7])],"isStart":false}),makeQuery(id+"F5.opExtrude","SWEPT_FACE",FACE,{"disambiguationData":[OSD([subQ7])]}),makeQuery(id+"F6.opExtrude","SWEPT_FACE",FACE,{"disambiguationData":[OSD([subQ6]),TDD([makeQuery(id+"F1.imprint","IMPRINT",EDGE,{"disambiguationData":[TD([[makeQuery(id+"F1.imprint","INTERSECT",VERTEX,{"derivedFrom":[subQ6,subQ5]}),1.0]])],"derivedFrom":subQ6})])]}),makeQuery(id+"F6.opExtrude","CAP_FACE",FACE,{"disambiguationData":[OSD([subQ6,subQ5,subQ4,subQ3,subQ2,subQ1,subQ0])],"isStart":false}),makeQuery(id+"F6.opExtrude","SWEPT_FACE",FACE,{"disambiguationData":[OSD([subQ6]),TDD([makeQuery(id+"F1.imprint","IMPRINT",EDGE,{"disambiguationData":[TD([[makeQuery(id+"F1.imprint","INTERSECT",VERTEX,{"derivedFrom":[subQ6,subQ16]}),-1.0]])],"derivedFrom":subQ6})])]}),makeQuery(id+"F6.opExtrude","CAP_FACE",FACE,{"disambiguationData":[OSD([subQ6,subQ16,subQ17,subQ3,subQ2,subQ19,subQ18])],"isStart":false}),makeQuery(id+"F7.opExtrude","SWEPT_FACE",FACE,{"disambiguationData":[OSD([subQ6]),TDD([makeQuery(id+"F1.imprint","IMPRINT",EDGE,{"disambiguationData":[TD([[makeQuery(id+"F1.imprint","INTERSECT",VERTEX,{"derivedFrom":[subQ6,subQ1]}),-1.0]])],"derivedFrom":subQ6})])]}),makeQuery(id+"F7.opExtrude","CAP_FACE",FACE,{"disambiguationData":[OSD([subQ6,subQ1,subQ0,subQ19,subQ18])],"isStart":false}),makeQuery(id+"F7.opExtrude","SWEPT_FACE",FACE,{"disambiguationData":[OSD([subQ6]),TDD([makeQuery(id+"F1.imprint","IMPRINT",EDGE,{"disambiguationData":[TD([[makeQuery(id+"F1.imprint","INTERSECT",VERTEX,{"derivedFrom":[subQ6,subQ0]}),1.0]])],"derivedFrom":subQ6})])]})]),OD(1.0)],"derivedFrom":makeQuery(id+"F7.opExtrude","SWEPT_FACE",FACE,{"disambiguationData":[OSD([subQ19,subQ18])]})});}
            var sketch = newSketch(context, id + "F8", { "sketchPlane" : qUnion([Q0])});
            skLineSegment(sketch, "E42", {"start": v(-48.04, 12.7) * mm, "end": v(-7.66, 50.8) * mm});
            skLineSegment(sketch, "E43", {"start": v(-7.66, 50.8) * mm, "end": v(-7.66, 65.35) * mm});
            skLineSegment(sketch, "E44", {"start": v(-7.66, 65.35) * mm, "end": v(-55.92, 65.35) * mm});
            skLineSegment(sketch, "E45", {"start": v(-55.92, 65.35) * mm, "end": v(-55.51, 12.7) * mm});
            skLineSegment(sketch, "E46", {"start": v(-55.51, 12.7) * mm, "end": v(-48.04, 12.7) * mm});
            skSolve(sketch);
        }
        {
            var Q0;
            {var subQ0=sQuery(id+"F1.wireOp",EDGE,"E20");var subQ1=sQuery(id+"F1.wireOp",EDGE,"E19");var subQ2=sQuery(id+"F1.wireOp",EDGE,"E18");var subQ3=sQuery(id+"F1.wireOp",EDGE,"E17");var subQ4=sQuery(id+"F1.wireOp",EDGE,"E7");var subQ5=sQuery(id+"F1.wireOp",EDGE,"E6");var subQ6=sQuery(id+"F1.wireOp",EDGE,"E0");var subQ7=sQuery(id+"F1.wireOp",EDGE,"E14");var subQ8=sQuery(id+"F1.wireOp",EDGE,"E15.trimOffspring");var subQ9=sQuery(id+"F1.wireOp",EDGE,"E12");var subQ10=sQuery(id+"F1.wireOp",EDGE,"E11.trimOffspring");var subQ11=sQuery(id+"F1.wireOp",EDGE,"E1");var subQ12=sQuery(id+"F1.wireOp",EDGE,"E16.trimOffspring");var subQ13=sQuery(id+"F1.wireOp",EDGE,"E13");var subQ14=sQuery(id+"F1.wireOp",EDGE,"E10.trimOffspring");var subQ15=sQuery(id+"F1.wireOp",EDGE,"E2");var subQ16=sQuery(id+"F1.wireOp",EDGE,"E4");var subQ17=sQuery(id+"F1.wireOp",EDGE,"E5");var subQ18=sQuery(id+"F1.wireOp",EDGE,"E22");var subQ19=sQuery(id+"F1.wireOp",EDGE,"E21");Q0=makeQuery(id+"F7.boolean.opBoolean","SPLIT",FACE,{"disambiguationData":[TD([makeQuery(id+"F2.opExtrude","SWEPT_FACE",FACE,{"disambiguationData":[OSD([subQ6])]}),makeQuery(id+"F2.opExtrude","CAP_FACE",FACE,{"disambiguationData":[OSD([subQ6,subQ11,subQ10,subQ9,subQ8])],"isStart":false}),makeQuery(id+"F3.opExtrude","CAP_FACE",FACE,{"disambiguationData":[OSD([subQ11,subQ15,subQ14,subQ10,subQ9,subQ13,subQ8,subQ12])],"isStart":false}),makeQuery(id+"F3.opExtrude","SWEPT_FACE",FACE,{"disambiguationData":[OSD([subQ11,subQ10,subQ9,subQ8])]}),makeQuery(id+"F4.opExtrude","CAP_FACE",FACE,{"disambiguationData":[OSD([subQ15,subQ14,subQ13,subQ7,subQ12])],"isStart":false}),makeQuery(id+"F4.opExtrude","SWEPT_FACE",FACE,{"disambiguationData":[OSD([subQ15,subQ14,subQ13,subQ12])]}),makeQuery(id+"F5.opExtrude","CAP_FACE",FACE,{"disambiguationData":[OSD([sQuery(id+"F1.wireOp",EDGE,"E3"),subQ7])],"isStart":false}),makeQuery(id+"F5.opExtrude","SWEPT_FACE",FACE,{"disambiguationData":[OSD([subQ7])]}),makeQuery(id+"F6.opExtrude","SWEPT_FACE",FACE,{"disambiguationData":[OSD([subQ6]),TDD([makeQuery(id+"F1.imprint","IMPRINT",EDGE,{"disambiguationData":[TD([[makeQuery(id+"F1.imprint","INTERSECT",VERTEX,{"derivedFrom":[subQ6,subQ5]}),1.0]])],"derivedFrom":subQ6})])]}),makeQuery(id+"F6.opExtrude","CAP_FACE",FACE,{"disambiguationData":[OSD([subQ6,subQ5,subQ4,subQ3,subQ2,subQ1,subQ0])],"isStart":false}),makeQuery(id+"F6.opExtrude","SWEPT_FACE",FACE,{"disambiguationData":[OSD([subQ6]),TDD([makeQuery(id+"F1.imprint","IMPRINT",EDGE,{"disambiguationData":[TD([[makeQuery(id+"F1.imprint","INTERSECT",VERTEX,{"derivedFrom":[subQ6,subQ16]}),-1.0]])],"derivedFrom":subQ6})])]}),makeQuery(id+"F6.opExtrude","CAP_FACE",FACE,{"disambiguationData":[OSD([subQ6,subQ16,subQ17,subQ3,subQ2,subQ19,subQ18])],"isStart":false}),makeQuery(id+"F7.opExtrude","SWEPT_FACE",FACE,{"disambiguationData":[OSD([subQ6]),TDD([makeQuery(id+"F1.imprint","IMPRINT",EDGE,{"disambiguationData":[TD([[makeQuery(id+"F1.imprint","INTERSECT",VERTEX,{"derivedFrom":[subQ6,subQ1]}),-1.0]])],"derivedFrom":subQ6})])]}),makeQuery(id+"F7.opExtrude","CAP_FACE",FACE,{"disambiguationData":[OSD([subQ6,subQ1,subQ0,subQ19,subQ18])],"isStart":false}),makeQuery(id+"F7.opExtrude","SWEPT_FACE",FACE,{"disambiguationData":[OSD([subQ6]),TDD([makeQuery(id+"F1.imprint","IMPRINT",EDGE,{"disambiguationData":[TD([[makeQuery(id+"F1.imprint","INTERSECT",VERTEX,{"derivedFrom":[subQ6,subQ0]}),1.0]])],"derivedFrom":subQ6})])]})]),OD(0.0)],"derivedFrom":makeQuery(id+"F7.opExtrude","SWEPT_FACE",FACE,{"disambiguationData":[OSD([subQ19,subQ18])]})});}
            var sketch = newSketch(context, id + "F9", { "sketchPlane" : qUnion([Q0])});
            skLineSegment(sketch, "E47", {"start": v(47.9, 12.7) * mm, "end": v(7.67, 50.8) * mm});
            skLineSegment(sketch, "E48", {"start": v(7.67, 50.8) * mm, "end": v(7.67, 53.93) * mm});
            skLineSegment(sketch, "E49", {"start": v(7.67, 53.93) * mm, "end": v(55.4, 55.84) * mm});
            skLineSegment(sketch, "E50", {"start": v(55.4, 55.84) * mm, "end": v(55.4, 12.7) * mm});
            skLineSegment(sketch, "E51", {"start": v(55.4, 12.7) * mm, "end": v(47.9, 12.7) * mm});
            skSolve(sketch);
        }
        {
            var Q0;
            {var subQ0=sQuery(id+"F1.wireOp",EDGE,"E18");var subQ4=sQuery(id+"F1.wireOp",EDGE,"E0");var subQ15=sQuery(id+"F1.wireOp",EDGE,"E5");Q0=makeQuery(id+"F6.boolean.opBoolean","SPLIT",FACE,{"disambiguationData":[TD([makeQuery(id+"F2.opExtrude","SWEPT_FACE",FACE,{"disambiguationData":[OSD([subQ4])]})])],"derivedFrom":makeQuery(id+"F6.opExtrude","SWEPT_FACE",FACE,{"disambiguationData":[OSD([subQ15,subQ0])]})});}
            var sketch = newSketch(context, id + "F10", { "sketchPlane" : qUnion([Q0])});
            skLineSegment(sketch, "E52", {"start": v(-47.8, 12.7) * mm, "end": v(-7.66, 50.8) * mm});
            skLineSegment(sketch, "E53", {"start": v(-7.66, 50.8) * mm, "end": v(-7.66, 52.64) * mm});
            skLineSegment(sketch, "E54", {"start": v(-7.66, 52.64) * mm, "end": v(-57.52, 52.64) * mm});
            skLineSegment(sketch, "E55", {"start": v(-57.52, 52.64) * mm, "end": v(-58.6, 12.7) * mm});
            skLineSegment(sketch, "E56", {"start": v(-58.6, 12.7) * mm, "end": v(-47.8, 12.7) * mm});
            skSolve(sketch);
        }
        {
            var Q0;
            Q0=qSketchRegion(id+"F8",true);
            extrude(context, id + "F11", {"entities" : qUnion([Q0]), "operationType" : NewBodyOperationType.REMOVE, "oppositeDirection" : true, "depth" : 15.24 * mm});
        }
        {
            var Q0;
            Q0=qSketchRegion(id+"F9",true);
            extrude(context, id + "F12", {"entities" : qUnion([Q0]), "operationType" : NewBodyOperationType.REMOVE, "oppositeDirection" : true, "depth" : 15.24 * mm});
        }
        {
            var Q0;
            Q0=qSketchRegion(id+"F10",true);
            extrude(context, id + "F13", {"entities" : qUnion([Q0]), "operationType" : NewBodyOperationType.REMOVE, "oppositeDirection" : true, "depth" : 15.24 * mm});
        }
        {
            var Q0;
            {var subQ0=sQuery(id+"F1.wireOp",EDGE,"E17");var subQ1=sQuery(id+"F1.wireOp",EDGE,"E7");var subQ2=sQuery(id+"F1.wireOp",EDGE,"E6");var subQ3=sQuery(id+"F1.wireOp",EDGE,"E5");var subQ4=sQuery(id+"F1.wireOp",EDGE,"E4");var subQ5=sQuery(id+"F1.wireOp",EDGE,"E0");var subQ6=sQuery(id+"F1.wireOp",EDGE,"E14");var subQ7=sQuery(id+"F1.wireOp",EDGE,"E15.trimOffspring");var subQ8=sQuery(id+"F1.wireOp",EDGE,"E12");var subQ9=sQuery(id+"F1.wireOp",EDGE,"E11.trimOffspring");var subQ10=sQuery(id+"F1.wireOp",EDGE,"E1");var subQ11=sQuery(id+"F1.wireOp",EDGE,"E16.trimOffspring");var subQ12=sQuery(id+"F1.wireOp",EDGE,"E13");var subQ13=sQuery(id+"F1.wireOp",EDGE,"E10.trimOffspring");var subQ14=sQuery(id+"F1.wireOp",EDGE,"E2");Q0=makeQuery(id+"F6.boolean.opBoolean","SPLIT",FACE,{"disambiguationData":[TD([makeQuery(id+"F2.opExtrude","SWEPT_FACE",FACE,{"disambiguationData":[OSD([subQ5])]}),makeQuery(id+"F2.opExtrude","CAP_FACE",FACE,{"disambiguationData":[OSD([subQ5,subQ10,subQ9,subQ8,subQ7])],"isStart":false}),makeQuery(id+"F3.opExtrude","CAP_FACE",FACE,{"disambiguationData":[OSD([subQ10,subQ14,subQ13,subQ9,subQ8,subQ12,subQ7,subQ11])],"isStart":false}),makeQuery(id+"F3.opExtrude","SWEPT_FACE",FACE,{"disambiguationData":[OSD([subQ10,subQ9,subQ8,subQ7])]}),makeQuery(id+"F4.opExtrude","CAP_FACE",FACE,{"disambiguationData":[OSD([subQ14,subQ13,subQ12,subQ6,subQ11])],"isStart":false}),makeQuery(id+"F4.opExtrude","SWEPT_FACE",FACE,{"disambiguationData":[OSD([subQ14,subQ13,subQ12,subQ11])]}),makeQuery(id+"F5.opExtrude","CAP_FACE",FACE,{"disambiguationData":[OSD([sQuery(id+"F1.wireOp",EDGE,"E3"),subQ6])],"isStart":false}),makeQuery(id+"F5.opExtrude","SWEPT_FACE",FACE,{"disambiguationData":[OSD([subQ6])]}),makeQuery(id+"F6.opExtrude","SWEPT_FACE",FACE,{"disambiguationData":[OSD([subQ5]),TDD([makeQuery(id+"F1.imprint","IMPRINT",EDGE,{"disambiguationData":[TD([[makeQuery(id+"F1.imprint","INTERSECT",VERTEX,{"derivedFrom":[subQ5,subQ2]}),1.0]])],"derivedFrom":subQ5})])]}),makeQuery(id+"F6.opExtrude","CAP_FACE",FACE,{"disambiguationData":[OSD([subQ5,subQ4,subQ3,subQ2,subQ1,subQ0,sQuery(id+"F1.wireOp",EDGE,"E18")])],"isStart":false}),makeQuery(id+"F6.opExtrude","SWEPT_FACE",FACE,{"disambiguationData":[OSD([subQ5]),TDD([makeQuery(id+"F1.imprint","IMPRINT",EDGE,{"disambiguationData":[TD([[makeQuery(id+"F1.imprint","INTERSECT",VERTEX,{"derivedFrom":[subQ5,subQ4]}),-1.0]])],"derivedFrom":subQ5})])]})]),OD(1.0)],"derivedFrom":makeQuery(id+"F6.opExtrude","SWEPT_FACE",FACE,{"disambiguationData":[OSD([subQ4,subQ2,subQ0])]})});}
            var sketch = newSketch(context, id + "F14", { "sketchPlane" : qUnion([Q0])});
            skLineSegment(sketch, "E57", {"start": v(-47.74, 12.7) * mm, "end": v(-7.65, 50.8) * mm});
            skLineSegment(sketch, "E58", {"start": v(-7.65, 50.8) * mm, "end": v(-7.65, 52.59) * mm});
            skLineSegment(sketch, "E59", {"start": v(-7.65, 52.59) * mm, "end": v(-58.24, 53.24) * mm});
            skLineSegment(sketch, "E60", {"start": v(-58.24, 53.24) * mm, "end": v(-54.04, 12.7) * mm});
            skLineSegment(sketch, "E61", {"start": v(-54.04, 12.7) * mm, "end": v(-47.74, 12.7) * mm});
            skPoint(sketch, "E62", {"position": v(-47, 12.7) * mm});
            skSolve(sketch);
        }
        {
            var Q0;
            Q0=qSketchRegion(id+"F14",true);
            extrude(context, id + "F15", {"entities" : qUnion([Q0]), "operationType" : NewBodyOperationType.REMOVE, "oppositeDirection" : true, "depth" : 15.24 * mm});
        }
        {
            var Q0;
            Q0=qCreatedBy(id+"F0.planeOp",FACE);
            var sketch = newSketch(context, id + "F16", { "sketchPlane" : qUnion([Q0])});
            skLineSegment(sketch, "E63.bottom", {"start": v(5.48, -3.8) * mm, "end": v(45.36, -3.8) * mm});
            skLineSegment(sketch, "E63.left", {"start": v(5.48, -3.8) * mm, "end": v(5.48, 3.81) * mm});
            skLineSegment(sketch, "E63.right", {"start": v(45.36, -3.8) * mm, "end": v(45.36, 3.81) * mm});
            skLineSegment(sketch, "E64.bottom", {"start": v(-5.62, -3.8) * mm, "end": v(-45.5, -3.81) * mm});
            skLineSegment(sketch, "E64.top", {"start": v(-5.62, 3.81) * mm, "end": v(-45.5, 3.8) * mm});
            skLineSegment(sketch, "E64.left", {"start": v(-5.62, -3.8) * mm, "end": v(-5.62, 3.81) * mm});
            skLineSegment(sketch, "E64.right", {"start": v(-45.5, -3.81) * mm, "end": v(-45.5, 3.8) * mm});
            skLineSegment(sketch, "E65.bottom", {"start": v(-3.81, 3.03) * mm, "end": v(3.8, 3.03) * mm});
            skLineSegment(sketch, "E65.top", {"start": v(-3.81, 45.2) * mm, "end": v(3.8, 45.2) * mm});
            skLineSegment(sketch, "E65.left", {"start": v(-3.8, 3.03) * mm, "end": v(-3.81, 45.2) * mm});
            skLineSegment(sketch, "E65.right", {"start": v(3.81, 3.03) * mm, "end": v(3.8, 45.2) * mm});
            skLineSegment(sketch, "E66.bottom", {"start": v(-3.81, -3.1) * mm, "end": v(3.8, -3.1) * mm});
            skLineSegment(sketch, "E66.top", {"start": v(-3.8, -45.25) * mm, "end": v(3.81, -45.25) * mm});
            skLineSegment(sketch, "E66.left", {"start": v(-3.81, -3.1) * mm, "end": v(-3.8, -45.25) * mm});
            skLineSegment(sketch, "E66.right", {"start": v(3.8, -3.1) * mm, "end": v(3.81, -45.25) * mm});
            skLineSegment(sketch, "E67", {"start": v(45.36, 3.81) * mm, "end": v(5.48, 3.81) * mm});
            skSolve(sketch);
        }
        {
            var Q0;
            Q0=qSketchRegion(id+"F16",true);
            extrude(context, id + "F17", {"entities" : qUnion([Q0]), "operationType" : NewBodyOperationType.REMOVE, "oppositeDirection" : true, "depth" : 47 * mm});
        }
        {
            var Q0;
            {var subQ0=sQuery(id+"F1.wireOp",EDGE,"E22");var subQ4=sQuery(id+"F1.wireOp",EDGE,"E3");var subQ5=makeQuery(id+"F1.imprint","INTERSECT",VERTEX,{"derivedFrom":[subQ4,subQ0]});Q0=makeQuery(id+"F1.imprint","IMPRINT",FACE,{"disambiguationData":[TD([[makeQuery(id+"F1.imprint","IMPRINT",EDGE,{"disambiguationData":[TD([[subQ5,-1.0]])],"derivedFrom":subQ4}),1.0]])]});}
            var Q1;
            {var subQ3=sQuery(id+"F1.wireOp",EDGE,"E3");var subQ5=sQuery(id+"F1.wireOp",EDGE,"E22");var subQ6=makeQuery(id+"F1.imprint","INTERSECT",VERTEX,{"derivedFrom":[subQ3,subQ5]});Q1=makeQuery(id+"F1.imprint","IMPRINT",FACE,{"disambiguationData":[TD([[makeQuery(id+"F1.imprint","IMPRINT",EDGE,{"disambiguationData":[TD([[subQ6,-1.0]])],"derivedFrom":subQ3}),-1.0]])]});}
            var Q2;
            {var subQ0=sQuery(id+"F1.wireOp",EDGE,"E22");var subQ1=sQuery(id+"F1.wireOp",EDGE,"E10.trimOffspring");var subQ2=makeQuery(id+"F1.imprint","INTERSECT",VERTEX,{"derivedFrom":[subQ1,subQ0]});Q2=makeQuery(id+"F1.imprint","IMPRINT",FACE,{"disambiguationData":[TD([[makeQuery(id+"F1.imprint","IMPRINT",EDGE,{"disambiguationData":[TD([[subQ2,-1.0]])],"derivedFrom":subQ1}),1.0]])]});}
            var Q3;
            {var subQ0=sQuery(id+"F1.wireOp",EDGE,"E22");var subQ1=sQuery(id+"F1.wireOp",EDGE,"E10.trimOffspring");var subQ2=makeQuery(id+"F1.imprint","INTERSECT",VERTEX,{"derivedFrom":[subQ1,subQ0]});Q3=makeQuery(id+"F1.imprint","IMPRINT",FACE,{"disambiguationData":[TD([[makeQuery(id+"F1.imprint","IMPRINT",EDGE,{"disambiguationData":[TD([[subQ2,-1.0]])],"derivedFrom":subQ1}),-1.0]])]});}
            var Q4;
            {var subQ0=sQuery(id+"F1.wireOp",EDGE,"E22");var subQ1=sQuery(id+"F1.wireOp",EDGE,"E0");var subQ2=makeQuery(id+"F1.imprint","INTERSECT",VERTEX,{"derivedFrom":[subQ1,subQ0]});Q4=makeQuery(id+"F1.imprint","IMPRINT",FACE,{"disambiguationData":[TD([[makeQuery(id+"F1.imprint","IMPRINT",EDGE,{"disambiguationData":[TD([[subQ2,-1.0]])],"derivedFrom":subQ1}),1.0]])]});}
            var Q5;
            {var subQ0=sQuery(id+"F1.wireOp",EDGE,"E17");var subQ3=sQuery(id+"F1.wireOp",EDGE,"E27");var subQ5=makeQuery(id+"F1.imprint","INTERSECT",VERTEX,{"derivedFrom":[subQ0,subQ3]});Q5=makeQuery(id+"F1.imprint","IMPRINT",FACE,{"disambiguationData":[TD([[makeQuery(id+"F1.imprint","IMPRINT",EDGE,{"disambiguationData":[TD([[subQ5,-1.0]])],"derivedFrom":subQ3}),1.0]])]});}
            var Q6;
            {var subQ0=sQuery(id+"F1.wireOp",EDGE,"E14");var subQ1=sQuery(id+"F1.wireOp",EDGE,"E4");var subQ2=makeQuery(id+"F1.imprint","INTERSECT",VERTEX,{"derivedFrom":[subQ1,subQ0]});Q6=makeQuery(id+"F1.imprint","IMPRINT",FACE,{"disambiguationData":[TD([[makeQuery(id+"F1.imprint","IMPRINT",EDGE,{"disambiguationData":[TD([[subQ2,1.0]])],"derivedFrom":subQ0}),1.0]])]});}
            var Q7;
            {var subQ1=sQuery(id+"F1.wireOp",EDGE,"E4");var subQ7=sQuery(id+"F1.wireOp",EDGE,"E31");var subQ9=makeQuery(id+"F1.imprint","INTERSECT",VERTEX,{"derivedFrom":[subQ1,subQ7]});Q7=makeQuery(id+"F1.imprint","IMPRINT",FACE,{"disambiguationData":[TD([[makeQuery(id+"F1.imprint","IMPRINT",EDGE,{"disambiguationData":[TD([[subQ9,1.0]])],"derivedFrom":subQ1}),-1.0]])]});}
            var Q8;
            {var subQ0=sQuery(id+"F1.wireOp",EDGE,"E28");var subQ1=sQuery(id+"F1.wireOp",EDGE,"E10.trimOffspring");var subQ2=makeQuery(id+"F1.imprint","INTERSECT",VERTEX,{"derivedFrom":[subQ1,subQ0]});Q8=makeQuery(id+"F1.imprint","IMPRINT",FACE,{"disambiguationData":[TD([[makeQuery(id+"F1.imprint","IMPRINT",EDGE,{"disambiguationData":[TD([[subQ2,-1.0]])],"derivedFrom":subQ1}),-1.0]])]});}
            var Q9;
            {var subQ0=sQuery(id+"F1.wireOp",EDGE,"E28");var subQ1=sQuery(id+"F1.wireOp",EDGE,"E0");var subQ2=makeQuery(id+"F1.imprint","INTERSECT",VERTEX,{"derivedFrom":[subQ1,subQ0]});Q9=makeQuery(id+"F1.imprint","IMPRINT",FACE,{"disambiguationData":[TD([[makeQuery(id+"F1.imprint","IMPRINT",EDGE,{"disambiguationData":[TD([[subQ2,-1.0]])],"derivedFrom":subQ1}),1.0]])]});}
            var Q10;
            {var subQ0=sQuery(id+"F1.wireOp",EDGE,"E32");var subQ1=sQuery(id+"F1.wireOp",EDGE,"E0");var subQ2=makeQuery(id+"F1.imprint","INTERSECT",VERTEX,{"derivedFrom":[subQ1,subQ0]});Q10=makeQuery(id+"F1.imprint","IMPRINT",FACE,{"disambiguationData":[TD([[makeQuery(id+"F1.imprint","IMPRINT",EDGE,{"disambiguationData":[TD([[subQ2,1.0]])],"derivedFrom":subQ1}),1.0]])]});}
            var Q11;
            {var subQ0=sQuery(id+"F1.wireOp",EDGE,"E19");var subQ1=sQuery(id+"F1.wireOp",EDGE,"E0");var subQ2=makeQuery(id+"F1.imprint","INTERSECT",VERTEX,{"derivedFrom":[subQ1,subQ0]});Q11=makeQuery(id+"F1.imprint","IMPRINT",FACE,{"disambiguationData":[TD([[makeQuery(id+"F1.imprint","IMPRINT",EDGE,{"disambiguationData":[TD([[subQ2,1.0]])],"derivedFrom":subQ1}),1.0]])]});}
            var Q12;
            {var subQ0=sQuery(id+"F1.wireOp",EDGE,"E33");var subQ1=sQuery(id+"F1.wireOp",EDGE,"E10.trimOffspring");var subQ2=makeQuery(id+"F1.imprint","INTERSECT",VERTEX,{"derivedFrom":[subQ1,subQ0]});Q12=makeQuery(id+"F1.imprint","IMPRINT",FACE,{"disambiguationData":[TD([[makeQuery(id+"F1.imprint","IMPRINT",EDGE,{"disambiguationData":[TD([[subQ2,-1.0]])],"derivedFrom":subQ1}),-1.0]])]});}
            var Q13;
            {var subQ0=sQuery(id+"F1.wireOp",EDGE,"E32");var subQ1=sQuery(id+"F1.wireOp",EDGE,"E10.trimOffspring");var subQ2=makeQuery(id+"F1.imprint","INTERSECT",VERTEX,{"derivedFrom":[subQ1,subQ0]});Q13=makeQuery(id+"F1.imprint","IMPRINT",FACE,{"disambiguationData":[TD([[makeQuery(id+"F1.imprint","IMPRINT",EDGE,{"disambiguationData":[TD([[subQ2,-1.0]])],"derivedFrom":subQ1}),-1.0]])]});}
            var Q14;
            {var subQ5=sQuery(id+"F1.wireOp",EDGE,"E6");var subQ7=sQuery(id+"F1.wireOp",EDGE,"E33");var subQ9=makeQuery(id+"F1.imprint","INTERSECT",VERTEX,{"derivedFrom":[subQ5,subQ7]});Q14=makeQuery(id+"F1.imprint","IMPRINT",FACE,{"disambiguationData":[TD([[makeQuery(id+"F1.imprint","IMPRINT",EDGE,{"disambiguationData":[TD([[subQ9,1.0]])],"derivedFrom":subQ5}),1.0]])]});}
            var Q15;
            {var subQ0=sQuery(id+"F1.wireOp",EDGE,"E32");var subQ1=sQuery(id+"F1.wireOp",EDGE,"E10.trimOffspring");var subQ2=makeQuery(id+"F1.imprint","INTERSECT",VERTEX,{"derivedFrom":[subQ1,subQ0]});Q15=makeQuery(id+"F1.imprint","IMPRINT",FACE,{"disambiguationData":[TD([[makeQuery(id+"F1.imprint","IMPRINT",EDGE,{"disambiguationData":[TD([[subQ2,-1.0]])],"derivedFrom":subQ1}),1.0]])]});}
            var Q16;
            {var subQ0=sQuery(id+"F1.wireOp",EDGE,"E6");var subQ5=sQuery(id+"F1.wireOp",EDGE,"E14");var subQ6=makeQuery(id+"F1.imprint","INTERSECT",VERTEX,{"derivedFrom":[subQ0,subQ5]});Q16=makeQuery(id+"F1.imprint","IMPRINT",FACE,{"disambiguationData":[TD([[makeQuery(id+"F1.imprint","IMPRINT",EDGE,{"disambiguationData":[TD([[subQ6,-1.0]])],"derivedFrom":subQ5}),1.0]])]});}
            var Q17;
            {var subQ0=sQuery(id+"F1.wireOp",EDGE,"E32");var subQ1=sQuery(id+"F1.wireOp",EDGE,"E3");var subQ2=makeQuery(id+"F1.imprint","INTERSECT",VERTEX,{"derivedFrom":[subQ1,subQ0]});Q17=makeQuery(id+"F1.imprint","IMPRINT",FACE,{"disambiguationData":[TD([[makeQuery(id+"F1.imprint","IMPRINT",EDGE,{"disambiguationData":[TD([[subQ2,-1.0]])],"derivedFrom":subQ1}),-1.0]])]});}
            var Q18;
            {var subQ5=sQuery(id+"F1.wireOp",EDGE,"E32");var subQ7=sQuery(id+"F1.wireOp",EDGE,"E3");var subQ8=makeQuery(id+"F1.imprint","INTERSECT",VERTEX,{"derivedFrom":[subQ7,subQ5]});Q18=makeQuery(id+"F1.imprint","IMPRINT",FACE,{"disambiguationData":[TD([[makeQuery(id+"F1.imprint","IMPRINT",EDGE,{"disambiguationData":[TD([[subQ8,-1.0]])],"derivedFrom":subQ7}),1.0]])]});}
            var Q19;
            {var subQ0=sQuery(id+"F1.wireOp",EDGE,"E17");var subQ3=sQuery(id+"F1.wireOp",EDGE,"E32");var subQ5=makeQuery(id+"F1.imprint","INTERSECT",VERTEX,{"derivedFrom":[subQ0,subQ3]});Q19=makeQuery(id+"F1.imprint","IMPRINT",FACE,{"disambiguationData":[TD([[makeQuery(id+"F1.imprint","IMPRINT",EDGE,{"disambiguationData":[TD([[subQ5,-1.0]])],"derivedFrom":subQ3}),-1.0]])]});}
            var Q20;
            {var subQ0=sQuery(id+"F1.wireOp",EDGE,"E18");var subQ3=sQuery(id+"F1.wireOp",EDGE,"E36");var subQ5=makeQuery(id+"F1.imprint","INTERSECT",VERTEX,{"derivedFrom":[subQ0,subQ3]});Q20=makeQuery(id+"F1.imprint","IMPRINT",FACE,{"disambiguationData":[TD([[makeQuery(id+"F1.imprint","IMPRINT",EDGE,{"disambiguationData":[TD([[subQ5,-1.0]])],"derivedFrom":subQ3}),-1.0]])]});}
            var Q21;
            {var subQ0=sQuery(id+"F1.wireOp",EDGE,"E5");var subQ5=sQuery(id+"F1.wireOp",EDGE,"E14");var subQ6=makeQuery(id+"F1.imprint","INTERSECT",VERTEX,{"derivedFrom":[subQ0,subQ5]});Q21=makeQuery(id+"F1.imprint","IMPRINT",FACE,{"disambiguationData":[TD([[makeQuery(id+"F1.imprint","IMPRINT",EDGE,{"disambiguationData":[TD([[subQ6,-1.0]])],"derivedFrom":subQ5}),1.0]])]});}
            var Q22;
            {var subQ0=sQuery(id+"F1.wireOp",EDGE,"E37");var subQ1=sQuery(id+"F1.wireOp",EDGE,"E1");var subQ2=makeQuery(id+"F1.imprint","INTERSECT",VERTEX,{"derivedFrom":[subQ1,subQ0]});Q22=makeQuery(id+"F1.imprint","IMPRINT",FACE,{"disambiguationData":[TD([[makeQuery(id+"F1.imprint","IMPRINT",EDGE,{"disambiguationData":[TD([[subQ2,-1.0]])],"derivedFrom":subQ1}),1.0]])]});}
            var Q23;
            {var subQ1=sQuery(id+"F1.wireOp",EDGE,"E2");var subQ7=sQuery(id+"F1.wireOp",EDGE,"E37");var subQ9=makeQuery(id+"F1.imprint","INTERSECT",VERTEX,{"derivedFrom":[subQ1,subQ7]});Q23=makeQuery(id+"F1.imprint","IMPRINT",FACE,{"disambiguationData":[TD([[makeQuery(id+"F1.imprint","IMPRINT",EDGE,{"disambiguationData":[TD([[subQ9,-1.0]])],"derivedFrom":subQ1}),1.0]])]});}
            var Q24;
            {var subQ0=sQuery(id+"F1.wireOp",EDGE,"E36");var subQ1=sQuery(id+"F1.wireOp",EDGE,"E0");var subQ2=makeQuery(id+"F1.imprint","INTERSECT",VERTEX,{"derivedFrom":[subQ1,subQ0]});Q24=makeQuery(id+"F1.imprint","IMPRINT",FACE,{"disambiguationData":[TD([[makeQuery(id+"F1.imprint","IMPRINT",EDGE,{"disambiguationData":[TD([[subQ2,1.0]])],"derivedFrom":subQ1}),1.0]])]});}
            var Q25;
            {var subQ5=sQuery(id+"F1.wireOp",EDGE,"E36");var subQ7=sQuery(id+"F1.wireOp",EDGE,"E3");var subQ9=makeQuery(id+"F1.imprint","INTERSECT",VERTEX,{"derivedFrom":[subQ7,subQ5]});Q25=makeQuery(id+"F1.imprint","IMPRINT",FACE,{"disambiguationData":[TD([[makeQuery(id+"F1.imprint","IMPRINT",EDGE,{"disambiguationData":[TD([[subQ9,-1.0]])],"derivedFrom":subQ7}),1.0]])]});}
            var Q26;
            {var subQ0=sQuery(id+"F1.wireOp",EDGE,"E36");var subQ1=sQuery(id+"F1.wireOp",EDGE,"E3");var subQ2=makeQuery(id+"F1.imprint","INTERSECT",VERTEX,{"derivedFrom":[subQ1,subQ0]});Q26=makeQuery(id+"F1.imprint","IMPRINT",FACE,{"disambiguationData":[TD([[makeQuery(id+"F1.imprint","IMPRINT",EDGE,{"disambiguationData":[TD([[subQ2,-1.0]])],"derivedFrom":subQ1}),-1.0]])]});}
            var Q27;
            {var subQ0=sQuery(id+"F1.wireOp",EDGE,"E36");var subQ1=sQuery(id+"F1.wireOp",EDGE,"E2");var subQ2=makeQuery(id+"F1.imprint","INTERSECT",VERTEX,{"derivedFrom":[subQ1,subQ0]});Q27=makeQuery(id+"F1.imprint","IMPRINT",FACE,{"disambiguationData":[TD([[makeQuery(id+"F1.imprint","IMPRINT",EDGE,{"disambiguationData":[TD([[subQ2,-1.0]])],"derivedFrom":subQ1}),1.0]])]});}
            var Q28;
            {var subQ0=sQuery(id+"F1.wireOp",EDGE,"E36");var subQ1=sQuery(id+"F1.wireOp",EDGE,"E1");var subQ2=makeQuery(id+"F1.imprint","INTERSECT",VERTEX,{"derivedFrom":[subQ1,subQ0]});Q28=makeQuery(id+"F1.imprint","IMPRINT",FACE,{"disambiguationData":[TD([[makeQuery(id+"F1.imprint","IMPRINT",EDGE,{"disambiguationData":[TD([[subQ2,-1.0]])],"derivedFrom":subQ1}),1.0]])]});}
            var Q29;
            {var subQ0=sQuery(id+"F1.wireOp",EDGE,"E21");var subQ1=sQuery(id+"F1.wireOp",EDGE,"E0");var subQ2=makeQuery(id+"F1.imprint","INTERSECT",VERTEX,{"derivedFrom":[subQ1,subQ0]});Q29=makeQuery(id+"F1.imprint","IMPRINT",FACE,{"disambiguationData":[TD([[makeQuery(id+"F1.imprint","IMPRINT",EDGE,{"disambiguationData":[TD([[subQ2,1.0]])],"derivedFrom":subQ1}),1.0]])]});}
            var Q30;
            {var subQ5=sQuery(id+"F1.wireOp",EDGE,"E35");var subQ7=sQuery(id+"F1.wireOp",EDGE,"E3");var subQ8=makeQuery(id+"F1.imprint","INTERSECT",VERTEX,{"derivedFrom":[subQ7,subQ5]});Q30=makeQuery(id+"F1.imprint","IMPRINT",FACE,{"disambiguationData":[TD([[makeQuery(id+"F1.imprint","IMPRINT",EDGE,{"disambiguationData":[TD([[subQ8,1.0]])],"derivedFrom":subQ7}),1.0]])]});}
            var Q31;
            {var subQ0=sQuery(id+"F1.wireOp",EDGE,"E35");var subQ1=sQuery(id+"F1.wireOp",EDGE,"E3");var subQ2=makeQuery(id+"F1.imprint","INTERSECT",VERTEX,{"derivedFrom":[subQ1,subQ0]});Q31=makeQuery(id+"F1.imprint","IMPRINT",FACE,{"disambiguationData":[TD([[makeQuery(id+"F1.imprint","IMPRINT",EDGE,{"disambiguationData":[TD([[subQ2,1.0]])],"derivedFrom":subQ1}),-1.0]])]});}
            var Q32;
            {var subQ0=sQuery(id+"F1.wireOp",EDGE,"E20");var subQ1=sQuery(id+"F1.wireOp",EDGE,"E2");var subQ2=makeQuery(id+"F1.imprint","INTERSECT",VERTEX,{"derivedFrom":[subQ1,subQ0]});Q32=makeQuery(id+"F1.imprint","IMPRINT",FACE,{"disambiguationData":[TD([[makeQuery(id+"F1.imprint","IMPRINT",EDGE,{"disambiguationData":[TD([[subQ2,-1.0]])],"derivedFrom":subQ1}),1.0]])]});}
            var Q33;
            {var subQ0=sQuery(id+"F1.wireOp",EDGE,"E20");var subQ1=sQuery(id+"F1.wireOp",EDGE,"E1");var subQ2=makeQuery(id+"F1.imprint","INTERSECT",VERTEX,{"derivedFrom":[subQ1,subQ0]});Q33=makeQuery(id+"F1.imprint","IMPRINT",FACE,{"disambiguationData":[TD([[makeQuery(id+"F1.imprint","IMPRINT",EDGE,{"disambiguationData":[TD([[subQ2,-1.0]])],"derivedFrom":subQ1}),1.0]])]});}
            var Q34;
            {var subQ0=sQuery(id+"F1.wireOp",EDGE,"E20");var subQ1=sQuery(id+"F1.wireOp",EDGE,"E0");var subQ2=makeQuery(id+"F1.imprint","INTERSECT",VERTEX,{"derivedFrom":[subQ1,subQ0]});Q34=makeQuery(id+"F1.imprint","IMPRINT",FACE,{"disambiguationData":[TD([[makeQuery(id+"F1.imprint","IMPRINT",EDGE,{"disambiguationData":[TD([[subQ2,-1.0]])],"derivedFrom":subQ1}),1.0]])]});}
            var Q35;
            {var subQ0=sQuery(id+"F1.wireOp",EDGE,"E34");var subQ1=sQuery(id+"F1.wireOp",EDGE,"E0");var subQ2=makeQuery(id+"F1.imprint","INTERSECT",VERTEX,{"derivedFrom":[subQ1,subQ0]});Q35=makeQuery(id+"F1.imprint","IMPRINT",FACE,{"disambiguationData":[TD([[makeQuery(id+"F1.imprint","IMPRINT",EDGE,{"disambiguationData":[TD([[subQ2,1.0]])],"derivedFrom":subQ1}),1.0]])]});}
            var Q36;
            {var subQ0=sQuery(id+"F1.wireOp",EDGE,"E35");var subQ1=sQuery(id+"F1.wireOp",EDGE,"E1");var subQ2=makeQuery(id+"F1.imprint","INTERSECT",VERTEX,{"derivedFrom":[subQ1,subQ0]});Q36=makeQuery(id+"F1.imprint","IMPRINT",FACE,{"disambiguationData":[TD([[makeQuery(id+"F1.imprint","IMPRINT",EDGE,{"disambiguationData":[TD([[subQ2,-1.0]])],"derivedFrom":subQ1}),1.0]])]});}
            var Q37;
            {var subQ3=sQuery(id+"F1.wireOp",EDGE,"E2");var subQ5=sQuery(id+"F1.wireOp",EDGE,"E35");var subQ6=makeQuery(id+"F1.imprint","INTERSECT",VERTEX,{"derivedFrom":[subQ3,subQ5]});Q37=makeQuery(id+"F1.imprint","IMPRINT",FACE,{"disambiguationData":[TD([[makeQuery(id+"F1.imprint","IMPRINT",EDGE,{"disambiguationData":[TD([[subQ6,-1.0]])],"derivedFrom":subQ3}),1.0]])]});}
            var Q38;
            {var subQ0=sQuery(id+"F1.wireOp",EDGE,"E7");var subQ5=sQuery(id+"F1.wireOp",EDGE,"E14");var subQ7=makeQuery(id+"F1.imprint","INTERSECT",VERTEX,{"derivedFrom":[subQ0,subQ5]});Q38=makeQuery(id+"F1.imprint","IMPRINT",FACE,{"disambiguationData":[TD([[makeQuery(id+"F1.imprint","IMPRINT",EDGE,{"disambiguationData":[TD([[subQ7,1.0]])],"derivedFrom":subQ5}),1.0]])]});}
            var Q39;
            {var subQ0=sQuery(id+"F1.wireOp",EDGE,"E18");var subQ3=sQuery(id+"F1.wireOp",EDGE,"E35");var subQ5=makeQuery(id+"F1.imprint","INTERSECT",VERTEX,{"derivedFrom":[subQ0,subQ3]});Q39=makeQuery(id+"F1.imprint","IMPRINT",FACE,{"disambiguationData":[TD([[makeQuery(id+"F1.imprint","IMPRINT",EDGE,{"disambiguationData":[TD([[subQ5,-1.0]])],"derivedFrom":subQ3}),1.0]])]});}
            var Q40;
            {var subQ0=sQuery(id+"F1.wireOp",EDGE,"E35");var subQ1=sQuery(id+"F1.wireOp",EDGE,"E2");var subQ2=makeQuery(id+"F1.imprint","INTERSECT",VERTEX,{"derivedFrom":[subQ1,subQ0]});Q40=makeQuery(id+"F1.imprint","IMPRINT",FACE,{"disambiguationData":[TD([[makeQuery(id+"F1.imprint","IMPRINT",EDGE,{"disambiguationData":[TD([[subQ2,-1.0]])],"derivedFrom":subQ1}),-1.0]])]});}
            var Q41;
            {var subQ4=sQuery(id+"F1.wireOp",EDGE,"E20");var subQ5=sQuery(id+"F1.wireOp",EDGE,"E2");var subQ6=makeQuery(id+"F1.imprint","INTERSECT",VERTEX,{"derivedFrom":[subQ5,subQ4]});Q41=makeQuery(id+"F1.imprint","IMPRINT",FACE,{"disambiguationData":[TD([[makeQuery(id+"F1.imprint","IMPRINT",EDGE,{"disambiguationData":[TD([[subQ6,-1.0]])],"derivedFrom":subQ5}),-1.0]])]});}
            var Q42;
            {var subQ0=sQuery(id+"F1.wireOp",EDGE,"E36");var subQ4=sQuery(id+"F1.wireOp",EDGE,"E2");var subQ5=makeQuery(id+"F1.imprint","INTERSECT",VERTEX,{"derivedFrom":[subQ4,subQ0]});Q42=makeQuery(id+"F1.imprint","IMPRINT",FACE,{"disambiguationData":[TD([[makeQuery(id+"F1.imprint","IMPRINT",EDGE,{"disambiguationData":[TD([[subQ5,-1.0]])],"derivedFrom":subQ4}),-1.0]])]});}
            extrude(context, id + "F18", {"entities" : qUnion([Q0, Q1, Q2, Q3, Q4, Q5, Q6, Q7, Q8, Q9, Q10, Q11, Q12, Q13, Q14, Q15, Q16, Q17, Q18, Q19, Q20, Q21, Q22, Q23, Q24, Q25, Q26, Q27, Q28, Q29, Q30, Q31, Q32, Q33, Q34, Q35, Q36, Q37, Q38, Q39, Q40, Q41, Q42]), "operationType" : NewBodyOperationType.ADD, "depth" : 50.8 * mm});
        }
        {
            var Q0;
            Q0=qCreatedBy(id+"F0.planeOp",FACE);
            var sketch = newSketch(context, id + "F19", { "sketchPlane" : qUnion([Q0])});
            skLineSegment(sketch, "E68", {"start": v(-10.16, -10.16) * mm, "end": v(-10.16, -12.95) * mm});
            skLineSegment(sketch, "E69", {"start": v(-10.16, -10.16) * mm, "end": v(-38.1, -10.16) * mm});
            skLineSegment(sketch, "E70", {"start": v(-38.1, -10.16) * mm, "end": v(-38.1, -12.95) * mm});
            skLineSegment(sketch, "E71", {"start": v(-38.1, -12.95) * mm, "end": v(-10.16, -12.95) * mm});
            skLineSegment(sketch, "E72", {"start": v(-10.16, -15.5) * mm, "end": v(-10.16, -18.29) * mm});
            skLineSegment(sketch, "E73", {"start": v(-10.16, -15.5) * mm, "end": v(-38.1, -15.5) * mm});
            skLineSegment(sketch, "E74", {"start": v(-38.1, -15.5) * mm, "end": v(-38.1, -18.29) * mm});
            skLineSegment(sketch, "E75", {"start": v(-38.1, -18.29) * mm, "end": v(-10.16, -18.29) * mm});
            skLineSegment(sketch, "E76", {"start": v(-10.16, 10.16) * mm, "end": v(-38.1, 10.16) * mm});
            skLineSegment(sketch, "E77", {"start": v(-38.1, 10.16) * mm, "end": v(-38.1, 12.95) * mm});
            skLineSegment(sketch, "E78", {"start": v(-38.1, 12.95) * mm, "end": v(-10.16, 12.95) * mm});
            skLineSegment(sketch, "E79", {"start": v(-10.16, 12.95) * mm, "end": v(-10.16, 10.16) * mm});
            skLineSegment(sketch, "E80", {"start": v(-10.16, 15.5) * mm, "end": v(-10.16, 18.29) * mm});
            skLineSegment(sketch, "E81", {"start": v(-10.16, 18.29) * mm, "end": v(-38.1, 18.29) * mm});
            skLineSegment(sketch, "E82", {"start": v(-38.1, 18.29) * mm, "end": v(-38.1, 15.5) * mm});
            skLineSegment(sketch, "E83", {"start": v(-38.1, 15.5) * mm, "end": v(-10.16, 15.5) * mm});
            skLineSegment(sketch, "E84", {"start": v(10.16, 18.29) * mm, "end": v(38.1, 18.29) * mm});
            skLineSegment(sketch, "E85", {"start": v(38.1, 18.29) * mm, "end": v(38.1, 15.5) * mm});
            skLineSegment(sketch, "E86", {"start": v(38.1, 15.5) * mm, "end": v(10.16, 15.5) * mm});
            skLineSegment(sketch, "E87", {"start": v(10.16, 15.5) * mm, "end": v(10.16, 18.29) * mm});
            skLineSegment(sketch, "E88", {"start": v(10.16, 12.95) * mm, "end": v(38.1, 12.95) * mm});
            skLineSegment(sketch, "E89", {"start": v(38.1, 12.95) * mm, "end": v(38.1, 10.16) * mm});
            skLineSegment(sketch, "E90", {"start": v(38.1, 10.16) * mm, "end": v(10.16, 10.16) * mm});
            skLineSegment(sketch, "E91", {"start": v(10.16, 10.16) * mm, "end": v(10.16, 12.95) * mm});
            skLineSegment(sketch, "E92", {"start": v(10.16, -10.16) * mm, "end": v(38.1, -10.16) * mm});
            skLineSegment(sketch, "E93", {"start": v(38.1, -10.16) * mm, "end": v(38.1, -12.95) * mm});
            skLineSegment(sketch, "E94", {"start": v(38.1, -12.95) * mm, "end": v(10.16, -12.95) * mm});
            skLineSegment(sketch, "E95", {"start": v(10.16, -12.95) * mm, "end": v(10.16, -10.16) * mm});
            skLineSegment(sketch, "E96", {"start": v(10.16, -15.5) * mm, "end": v(38.1, -15.5) * mm});
            skLineSegment(sketch, "E97", {"start": v(38.1, -15.5) * mm, "end": v(38.1, -18.29) * mm});
            skLineSegment(sketch, "E98", {"start": v(38.1, -18.29) * mm, "end": v(10.16, -18.29) * mm});
            skLineSegment(sketch, "E99", {"start": v(10.16, -18.29) * mm, "end": v(10.16, -15.5) * mm});
            skLineSegment(sketch, "E100", {"start": v(-10.16, 20.83) * mm, "end": v(-38.1, 20.83) * mm});
            skLineSegment(sketch, "E101", {"start": v(-10.16, 20.83) * mm, "end": v(-10.16, 23.62) * mm});
            skLineSegment(sketch, "E102", {"start": v(-10.16, 23.62) * mm, "end": v(-38.1, 23.62) * mm});
            skLineSegment(sketch, "E103", {"start": v(-38.1, 23.62) * mm, "end": v(-38.1, 20.83) * mm});
            skLineSegment(sketch, "E104", {"start": v(-10.16, 26.16) * mm, "end": v(-38.1, 26.16) * mm});
            skLineSegment(sketch, "E105", {"start": v(-38.1, 26.16) * mm, "end": v(-38.1, 28.96) * mm});
            skLineSegment(sketch, "E106", {"start": v(-38.1, 28.96) * mm, "end": v(-10.16, 28.96) * mm});
            skLineSegment(sketch, "E107", {"start": v(-10.16, 28.96) * mm, "end": v(-10.16, 26.16) * mm});
            skLineSegment(sketch, "E108.bottom", {"start": v(-10.16, -20.83) * mm, "end": v(-38.1, -20.83) * mm});
            skLineSegment(sketch, "E108.top", {"start": v(-10.16, -23.62) * mm, "end": v(-38.1, -23.62) * mm});
            skLineSegment(sketch, "E108.left", {"start": v(-10.16, -20.83) * mm, "end": v(-10.16, -23.62) * mm});
            skLineSegment(sketch, "E108.right", {"start": v(-38.1, -20.83) * mm, "end": v(-38.1, -23.62) * mm});
            skLineSegment(sketch, "E109.bottom", {"start": v(-10.16, -26.16) * mm, "end": v(-38.1, -26.16) * mm});
            skLineSegment(sketch, "E109.top", {"start": v(-10.16, -28.96) * mm, "end": v(-38.1, -28.96) * mm});
            skLineSegment(sketch, "E109.left", {"start": v(-10.16, -26.16) * mm, "end": v(-10.16, -28.96) * mm});
            skLineSegment(sketch, "E109.right", {"start": v(-38.1, -26.16) * mm, "end": v(-38.1, -28.96) * mm});
            skLineSegment(sketch, "E110.bottom", {"start": v(10.16, -20.83) * mm, "end": v(38.1, -20.83) * mm});
            skLineSegment(sketch, "E110.top", {"start": v(10.16, -23.62) * mm, "end": v(38.1, -23.62) * mm});
            skLineSegment(sketch, "E110.left", {"start": v(10.16, -20.83) * mm, "end": v(10.16, -23.62) * mm});
            skLineSegment(sketch, "E110.right", {"start": v(38.1, -20.83) * mm, "end": v(38.1, -23.62) * mm});
            skLineSegment(sketch, "E111.bottom", {"start": v(10.16, -26.16) * mm, "end": v(38.1, -26.16) * mm});
            skLineSegment(sketch, "E111.top", {"start": v(10.16, -28.96) * mm, "end": v(38.1, -28.96) * mm});
            skLineSegment(sketch, "E111.left", {"start": v(10.16, -26.16) * mm, "end": v(10.16, -28.96) * mm});
            skLineSegment(sketch, "E111.right", {"start": v(38.1, -26.16) * mm, "end": v(38.1, -28.96) * mm});
            skLineSegment(sketch, "E112.bottom", {"start": v(10.16, 20.83) * mm, "end": v(38.1, 20.83) * mm});
            skLineSegment(sketch, "E112.top", {"start": v(10.16, 23.62) * mm, "end": v(38.1, 23.62) * mm});
            skLineSegment(sketch, "E112.left", {"start": v(10.16, 20.83) * mm, "end": v(10.16, 23.62) * mm});
            skLineSegment(sketch, "E112.right", {"start": v(38.1, 20.83) * mm, "end": v(38.1, 23.62) * mm});
            skLineSegment(sketch, "E113.bottom", {"start": v(10.16, 26.16) * mm, "end": v(38.1, 26.16) * mm});
            skLineSegment(sketch, "E113.top", {"start": v(10.16, 28.96) * mm, "end": v(38.1, 28.96) * mm});
            skLineSegment(sketch, "E113.left", {"start": v(10.16, 26.16) * mm, "end": v(10.16, 28.96) * mm});
            skLineSegment(sketch, "E113.right", {"start": v(38.1, 26.16) * mm, "end": v(38.1, 28.96) * mm});
            skSolve(sketch);
        }
        {
            var Q0;
            Q0=makeQuery(id+"F18.opExtrude","SWEPT_FACE",FACE,{"disambiguationData":[OSD([sQuery(id+"F1.wireOp",EDGE,"E31")])]});
            var sketch = newSketch(context, id + "F20", { "sketchPlane" : qUnion([Q0])});
            skLineSegment(sketch, "E114", {"start": v(-7.62, 50.8) * mm, "end": v(-39.37, 12.7) * mm});
            skLineSegment(sketch, "E115", {"start": v(-39.37, 12.7) * mm, "end": v(-60.1, 12.7) * mm});
            skLineSegment(sketch, "E116", {"start": v(-60.1, 12.7) * mm, "end": v(-60.1, 65.61) * mm});
            skLineSegment(sketch, "E117", {"start": v(-60.1, 65.61) * mm, "end": v(-7.62, 65.61) * mm});
            skLineSegment(sketch, "E118", {"start": v(-7.62, 65.61) * mm, "end": v(-7.62, 50.8) * mm});
            skSolve(sketch);
        }
        {
            var Q0;
            Q0=qSketchRegion(id+"F20",true);
            extrude(context, id + "F21", {"entities" : qUnion([Q0]), "operationType" : NewBodyOperationType.REMOVE, "oppositeDirection" : true, "depth" : 24.49 * mm});
        }
        {
            var Q0;
            Q0=qSketchRegion(id+"F19",true);
            extrude(context, id + "F22", {"entities" : qUnion([Q0]), "operationType" : NewBodyOperationType.REMOVE, "oppositeDirection" : true, "depth" : 47 * mm});
        }
        {
            var Q0;
            Q0=makeQuery(id+"F18.opExtrude","SWEPT_FACE",FACE,{"disambiguationData":[OSD([sQuery(id+"F1.wireOp",EDGE,"E33")])]});
            var sketch = newSketch(context, id + "F23", { "sketchPlane" : qUnion([Q0])});
            skLineSegment(sketch, "E119", {"start": v(7.62, 50.8) * mm, "end": v(39.37, 12.7) * mm});
            skLineSegment(sketch, "E120", {"start": v(39.37, 12.7) * mm, "end": v(63.4, 12.7) * mm});
            skLineSegment(sketch, "E121", {"start": v(63.4, 12.7) * mm, "end": v(63.4, 58.95) * mm});
            skLineSegment(sketch, "E122", {"start": v(63.4, 58.95) * mm, "end": v(7.62, 58.95) * mm});
            skLineSegment(sketch, "E123", {"start": v(7.62, 58.95) * mm, "end": v(7.62, 50.8) * mm});
            skSolve(sketch);
        }
        {
            var Q0;
            Q0=qSketchRegion(id+"F23",true);
            extrude(context, id + "F24", {"entities" : qUnion([Q0]), "operationType" : NewBodyOperationType.REMOVE, "oppositeDirection" : true, "depth" : 24.49 * mm});
        }
        {
            var Q0;
            Q0=makeQuery(id+"F18.opExtrude","SWEPT_FACE",FACE,{"disambiguationData":[OSD([sQuery(id+"F1.wireOp",EDGE,"E34")])]});
            var sketch = newSketch(context, id + "F25", { "sketchPlane" : qUnion([Q0])});
            skLineSegment(sketch, "E124", {"start": v(-7.62, 50.8) * mm, "end": v(-39.37, 12.7) * mm});
            skLineSegment(sketch, "E125", {"start": v(-39.37, 12.7) * mm, "end": v(-64.42, 12.7) * mm});
            skLineSegment(sketch, "E126", {"start": v(-64.42, 12.7) * mm, "end": v(-64.42, 60.83) * mm});
            skLineSegment(sketch, "E127", {"start": v(-64.42, 60.83) * mm, "end": v(-7.62, 60.83) * mm});
            skLineSegment(sketch, "E128", {"start": v(-7.62, 60.83) * mm, "end": v(-7.62, 50.8) * mm});
            skSolve(sketch);
        }
        {
            var Q0;
            Q0=qSketchRegion(id+"F25",true);
            extrude(context, id + "F26", {"entities" : qUnion([Q0]), "operationType" : NewBodyOperationType.REMOVE, "oppositeDirection" : true, "depth" : 24.49 * mm});
        }
        {
            var Q0;
            Q0=makeQuery(id+"F18.opExtrude","SWEPT_FACE",FACE,{"disambiguationData":[OSD([sQuery(id+"F1.wireOp",EDGE,"E37")])]});
            var sketch = newSketch(context, id + "F27", { "sketchPlane" : qUnion([Q0])});
            skLineSegment(sketch, "E129", {"start": v(7.62, 50.8) * mm, "end": v(39.37, 12.7) * mm});
            skLineSegment(sketch, "E130", {"start": v(39.37, 12.7) * mm, "end": v(79.1, 12.7) * mm});
            skLineSegment(sketch, "E131", {"start": v(79.1, 12.7) * mm, "end": v(79.1, 63.6) * mm});
            skLineSegment(sketch, "E132", {"start": v(79.1, 63.6) * mm, "end": v(7.62, 58.32) * mm});
            skLineSegment(sketch, "E133", {"start": v(7.62, 58.32) * mm, "end": v(7.62, 50.8) * mm});
            skSolve(sketch);
        }
        {
            var Q0;
            Q0=qSketchRegion(id+"F27",true);
            extrude(context, id + "F28", {"entities" : qUnion([Q0]), "operationType" : NewBodyOperationType.REMOVE, "oppositeDirection" : true, "depth" : 24.49 * mm});
        }
        {
            var Q0;
            {var subQ5=sQuery(id+"F1.wireOp",EDGE,"E29.trimOffspring");Q0=makeQuery(id+"F1.imprint","IMPRINT",FACE,{"disambiguationData":[TD([[makeQuery(id+"F1.imprint","IMPRINT",EDGE,{"derivedFrom":subQ5}),1.0]])]});}
            var Q1;
            {var subQ0=sQuery(id+"F1.wireOp",EDGE,"E29.trimOffspring");Q1=makeQuery(id+"F1.imprint","IMPRINT",FACE,{"disambiguationData":[TD([[makeQuery(id+"F1.imprint","IMPRINT",EDGE,{"derivedFrom":subQ0}),-1.0]])]});}
            var Q2;
            {var subQ0=sQuery(id+"F1.wireOp",EDGE,"E5");var subQ3=sQuery(id+"F1.wireOp",EDGE,"E37");var subQ5=makeQuery(id+"F1.imprint","INTERSECT",VERTEX,{"derivedFrom":[subQ0,subQ3]});Q2=makeQuery(id+"F1.imprint","IMPRINT",FACE,{"disambiguationData":[TD([[makeQuery(id+"F1.imprint","IMPRINT",EDGE,{"disambiguationData":[TD([[subQ5,-1.0]])],"derivedFrom":subQ3}),-1.0]])]});}
            var Q3;
            {var subQ1=sQuery(id+"F1.wireOp",EDGE,"E1");var subQ3=sQuery(id+"F1.wireOp",EDGE,"E34");var subQ4=makeQuery(id+"F1.imprint","INTERSECT",VERTEX,{"derivedFrom":[subQ1,subQ3]});Q3=makeQuery(id+"F1.imprint","IMPRINT",FACE,{"disambiguationData":[TD([[makeQuery(id+"F1.imprint","IMPRINT",EDGE,{"disambiguationData":[TD([[subQ4,1.0]])],"derivedFrom":subQ3}),1.0]])]});}
            var Q4;
            {var subQ0=sQuery(id+"F1.wireOp",EDGE,"E7");var subQ3=sQuery(id+"F1.wireOp",EDGE,"E34");var subQ5=makeQuery(id+"F1.imprint","INTERSECT",VERTEX,{"derivedFrom":[subQ0,subQ3]});Q4=makeQuery(id+"F1.imprint","IMPRINT",FACE,{"disambiguationData":[TD([[makeQuery(id+"F1.imprint","IMPRINT",EDGE,{"disambiguationData":[TD([[subQ5,-1.0]])],"derivedFrom":subQ3}),1.0]])]});}
            var Q5;
            {var subQ1=sQuery(id+"F1.wireOp",EDGE,"E6");var subQ3=sQuery(id+"F1.wireOp",EDGE,"E33");var subQ4=makeQuery(id+"F1.imprint","INTERSECT",VERTEX,{"derivedFrom":[subQ1,subQ3]});Q5=makeQuery(id+"F1.imprint","IMPRINT",FACE,{"disambiguationData":[TD([[makeQuery(id+"F1.imprint","IMPRINT",EDGE,{"disambiguationData":[TD([[subQ4,-1.0]])],"derivedFrom":subQ3}),-1.0]])]});}
            var Q6;
            {var subQ0=sQuery(id+"F1.wireOp",EDGE,"E19");var subQ1=sQuery(id+"F1.wireOp",EDGE,"E0");var subQ2=makeQuery(id+"F1.imprint","INTERSECT",VERTEX,{"derivedFrom":[subQ1,subQ0]});Q6=makeQuery(id+"F1.imprint","IMPRINT",FACE,{"disambiguationData":[TD([[makeQuery(id+"F1.imprint","IMPRINT",EDGE,{"disambiguationData":[TD([[subQ2,1.0]])],"derivedFrom":subQ1}),1.0]])]});}
            var Q7;
            {var subQ0=sQuery(id+"F1.wireOp",EDGE,"E22");var subQ1=sQuery(id+"F1.wireOp",EDGE,"E0");var subQ2=makeQuery(id+"F1.imprint","INTERSECT",VERTEX,{"derivedFrom":[subQ1,subQ0]});Q7=makeQuery(id+"F1.imprint","IMPRINT",FACE,{"disambiguationData":[TD([[makeQuery(id+"F1.imprint","IMPRINT",EDGE,{"disambiguationData":[TD([[subQ2,-1.0]])],"derivedFrom":subQ1}),1.0]])]});}
            var Q8;
            {var subQ0=sQuery(id+"F1.wireOp",EDGE,"E21");var subQ1=sQuery(id+"F1.wireOp",EDGE,"E0");var subQ2=makeQuery(id+"F1.imprint","INTERSECT",VERTEX,{"derivedFrom":[subQ1,subQ0]});Q8=makeQuery(id+"F1.imprint","IMPRINT",FACE,{"disambiguationData":[TD([[makeQuery(id+"F1.imprint","IMPRINT",EDGE,{"disambiguationData":[TD([[subQ2,1.0]])],"derivedFrom":subQ1}),1.0]])]});}
            var Q9;
            {var subQ0=sQuery(id+"F1.wireOp",EDGE,"E20");var subQ1=sQuery(id+"F1.wireOp",EDGE,"E0");var subQ2=makeQuery(id+"F1.imprint","INTERSECT",VERTEX,{"derivedFrom":[subQ1,subQ0]});Q9=makeQuery(id+"F1.imprint","IMPRINT",FACE,{"disambiguationData":[TD([[makeQuery(id+"F1.imprint","IMPRINT",EDGE,{"disambiguationData":[TD([[subQ2,-1.0]])],"derivedFrom":subQ1}),1.0]])]});}
            extrude(context, id + "F29", {"entities" : qUnion([Q0, Q1, Q2, Q3, Q4, Q5, Q6, Q7, Q8, Q9]), "operationType" : NewBodyOperationType.REMOVE, "endBound" : BoundingType.THROUGH_ALL, "depth" : 25.4 * mm});
        }
        {
            var Q0;
            {var subQ0=sQuery(id+"F1.wireOp",EDGE,"E7");var subQ1=sQuery(id+"F1.wireOp",EDGE,"E0");var subQ2=makeQuery(id+"F1.imprint","INTERSECT",VERTEX,{"derivedFrom":[subQ1,subQ0]});Q0=makeQuery(id+"F1.imprint","IMPRINT",FACE,{"disambiguationData":[TD([[makeQuery(id+"F1.imprint","IMPRINT",EDGE,{"disambiguationData":[TD([[subQ2,1.0]])],"derivedFrom":subQ1}),1.0]])]});}
            var Q1;
            {var subQ0=sQuery(id+"F1.wireOp",EDGE,"E6");var subQ1=sQuery(id+"F1.wireOp",EDGE,"E0");var subQ2=makeQuery(id+"F1.imprint","INTERSECT",VERTEX,{"derivedFrom":[subQ1,subQ0]});Q1=makeQuery(id+"F1.imprint","IMPRINT",FACE,{"disambiguationData":[TD([[makeQuery(id+"F1.imprint","IMPRINT",EDGE,{"disambiguationData":[TD([[subQ2,-1.0]])],"derivedFrom":subQ1}),1.0]])]});}
            var Q2;
            {var subQ0=sQuery(id+"F1.wireOp",EDGE,"E4");var subQ1=sQuery(id+"F1.wireOp",EDGE,"E0");var subQ2=makeQuery(id+"F1.imprint","INTERSECT",VERTEX,{"derivedFrom":[subQ1,subQ0]});Q2=makeQuery(id+"F1.imprint","IMPRINT",FACE,{"disambiguationData":[TD([[makeQuery(id+"F1.imprint","IMPRINT",EDGE,{"disambiguationData":[TD([[subQ2,1.0]])],"derivedFrom":subQ1}),1.0]])]});}
            var Q3;
            {var subQ0=sQuery(id+"F1.wireOp",EDGE,"E5");var subQ1=sQuery(id+"F1.wireOp",EDGE,"E0");var subQ2=makeQuery(id+"F1.imprint","INTERSECT",VERTEX,{"derivedFrom":[subQ1,subQ0]});Q3=makeQuery(id+"F1.imprint","IMPRINT",FACE,{"disambiguationData":[TD([[makeQuery(id+"F1.imprint","IMPRINT",EDGE,{"disambiguationData":[TD([[subQ2,-1.0]])],"derivedFrom":subQ1}),1.0]])]});}
            extrude(context, id + "F30", {"entities" : qUnion([Q0, Q1, Q2, Q3]), "operationType" : NewBodyOperationType.REMOVE, "depth" : 25.4 * mm});
        }
        {
            var Q0;
            {var subQ0=sQuery(id+"F1.wireOp",EDGE,"E16.trimOffspring");var subQ1=sQuery(id+"F1.wireOp",EDGE,"E13");var subQ2=sQuery(id+"F1.wireOp",EDGE,"E10.trimOffspring");var subQ3=sQuery(id+"F1.wireOp",EDGE,"E2");var subQ5=sQuery(id+"F1.wireOp",EDGE,"E40");var subQ7=sQuery(id+"F1.wireOp",EDGE,"E36");var subQ8=makeQuery(id+"F3.opExtrude","SWEPT_FACE",FACE,{"disambiguationData":[OSD([subQ7])]});var subQ9=sQuery(id+"F1.wireOp",EDGE,"E39.trimOffspring");var subQ10=sQuery(id+"F1.wireOp",EDGE,"E12");var subQ11=sQuery(id+"F1.wireOp",EDGE,"E1");var subQ18=sQuery(id+"F1.wireOp",EDGE,"E41.trimOffspring");var subQ19=sQuery(id+"F1.wireOp",EDGE,"E15.trimOffspring");var subQ20=sQuery(id+"F1.wireOp",EDGE,"E11.trimOffspring");var subQ21=sQuery(id+"F1.wireOp",EDGE,"E35");Q0=makeQuery(id+"F7.boolean.opBoolean","SPLIT",FACE,{"disambiguationData":[TD([subQ8])],"derivedFrom":makeQuery(id+"F6.boolean.opBoolean","SPLIT",FACE,{"disambiguationData":[TD([makeQuery(id+"F3.opExtrude","SWEPT_FACE",FACE,{"disambiguationData":[OSD([subQ21])]})])],"derivedFrom":makeQuery(id+"F3.opExtrude","CAP_FACE",FACE,{"disambiguationData":[OSD([subQ11,subQ3,subQ2,subQ20,subQ10,subQ1,subQ19,subQ0,sQuery(id+"F1.wireOp",EDGE,"E28"),sQuery(id+"F1.wireOp",EDGE,"E32"),subQ21,subQ7,sQuery(id+"F1.wireOp",EDGE,"E38"),subQ9,subQ5,subQ18])],"isStart":false})})});}
            var Q1;
            {var subQ0=sQuery(id+"F1.wireOp",EDGE,"E16.trimOffspring");var subQ1=sQuery(id+"F1.wireOp",EDGE,"E13");var subQ2=sQuery(id+"F1.wireOp",EDGE,"E10.trimOffspring");var subQ3=sQuery(id+"F1.wireOp",EDGE,"E2");var subQ5=sQuery(id+"F1.wireOp",EDGE,"E38");var subQ7=sQuery(id+"F1.wireOp",EDGE,"E28");var subQ8=makeQuery(id+"F3.opExtrude","SWEPT_FACE",FACE,{"disambiguationData":[OSD([subQ7])]});var subQ9=sQuery(id+"F1.wireOp",EDGE,"E39.trimOffspring");var subQ10=sQuery(id+"F1.wireOp",EDGE,"E12");var subQ11=sQuery(id+"F1.wireOp",EDGE,"E1");var subQ18=sQuery(id+"F1.wireOp",EDGE,"E32");var subQ19=sQuery(id+"F1.wireOp",EDGE,"E41.trimOffspring");var subQ20=sQuery(id+"F1.wireOp",EDGE,"E15.trimOffspring");var subQ21=sQuery(id+"F1.wireOp",EDGE,"E11.trimOffspring");Q1=makeQuery(id+"F7.boolean.opBoolean","SPLIT",FACE,{"disambiguationData":[TD([subQ8])],"derivedFrom":makeQuery(id+"F6.boolean.opBoolean","SPLIT",FACE,{"disambiguationData":[TD([subQ8])],"derivedFrom":makeQuery(id+"F3.opExtrude","CAP_FACE",FACE,{"disambiguationData":[OSD([subQ11,subQ3,subQ2,subQ21,subQ10,subQ1,subQ20,subQ0,subQ7,subQ18,sQuery(id+"F1.wireOp",EDGE,"E35"),sQuery(id+"F1.wireOp",EDGE,"E36"),subQ5,subQ9,sQuery(id+"F1.wireOp",EDGE,"E40"),subQ19])],"isStart":false})})});}
            var Q2;
            {var subQ0=sQuery(id+"F1.wireOp",EDGE,"E32");var subQ1=makeQuery(id+"F3.opExtrude","SWEPT_FACE",FACE,{"disambiguationData":[OSD([subQ0])]});var subQ3=sQuery(id+"F1.wireOp",EDGE,"E16.trimOffspring");var subQ4=sQuery(id+"F1.wireOp",EDGE,"E13");var subQ5=sQuery(id+"F1.wireOp",EDGE,"E10.trimOffspring");var subQ6=sQuery(id+"F1.wireOp",EDGE,"E2");var subQ8=sQuery(id+"F1.wireOp",EDGE,"E38");var subQ10=sQuery(id+"F1.wireOp",EDGE,"E41.trimOffspring");var subQ11=sQuery(id+"F1.wireOp",EDGE,"E15.trimOffspring");var subQ12=sQuery(id+"F1.wireOp",EDGE,"E11.trimOffspring");var subQ14=sQuery(id+"F1.wireOp",EDGE,"E28");var subQ15=sQuery(id+"F1.wireOp",EDGE,"E39.trimOffspring");var subQ16=sQuery(id+"F1.wireOp",EDGE,"E12");var subQ17=sQuery(id+"F1.wireOp",EDGE,"E1");Q2=makeQuery(id+"F7.boolean.opBoolean","SPLIT",FACE,{"disambiguationData":[TD([subQ1])],"derivedFrom":makeQuery(id+"F6.boolean.opBoolean","SPLIT",FACE,{"disambiguationData":[TD([makeQuery(id+"F3.opExtrude","SWEPT_FACE",FACE,{"disambiguationData":[OSD([subQ14])]})])],"derivedFrom":makeQuery(id+"F3.opExtrude","CAP_FACE",FACE,{"disambiguationData":[OSD([subQ17,subQ6,subQ5,subQ12,subQ16,subQ4,subQ11,subQ3,subQ14,subQ0,sQuery(id+"F1.wireOp",EDGE,"E35"),sQuery(id+"F1.wireOp",EDGE,"E36"),subQ8,subQ15,sQuery(id+"F1.wireOp",EDGE,"E40"),subQ10])],"isStart":false})})});}
            var Q3;
            {var subQ0=sQuery(id+"F1.wireOp",EDGE,"E40");var subQ2=sQuery(id+"F1.wireOp",EDGE,"E16.trimOffspring");var subQ3=sQuery(id+"F1.wireOp",EDGE,"E13");var subQ4=sQuery(id+"F1.wireOp",EDGE,"E10.trimOffspring");var subQ5=sQuery(id+"F1.wireOp",EDGE,"E2");var subQ7=sQuery(id+"F1.wireOp",EDGE,"E35");var subQ8=makeQuery(id+"F3.opExtrude","SWEPT_FACE",FACE,{"disambiguationData":[OSD([subQ7])]});var subQ10=sQuery(id+"F1.wireOp",EDGE,"E41.trimOffspring");var subQ11=sQuery(id+"F1.wireOp",EDGE,"E15.trimOffspring");var subQ12=sQuery(id+"F1.wireOp",EDGE,"E11.trimOffspring");var subQ14=sQuery(id+"F1.wireOp",EDGE,"E36");var subQ15=sQuery(id+"F1.wireOp",EDGE,"E39.trimOffspring");var subQ16=sQuery(id+"F1.wireOp",EDGE,"E12");var subQ17=sQuery(id+"F1.wireOp",EDGE,"E1");Q3=makeQuery(id+"F7.boolean.opBoolean","SPLIT",FACE,{"disambiguationData":[TD([subQ8])],"derivedFrom":makeQuery(id+"F6.boolean.opBoolean","SPLIT",FACE,{"disambiguationData":[TD([subQ8])],"derivedFrom":makeQuery(id+"F3.opExtrude","CAP_FACE",FACE,{"disambiguationData":[OSD([subQ17,subQ5,subQ4,subQ12,subQ16,subQ3,subQ11,subQ2,sQuery(id+"F1.wireOp",EDGE,"E28"),sQuery(id+"F1.wireOp",EDGE,"E32"),subQ7,subQ14,sQuery(id+"F1.wireOp",EDGE,"E38"),subQ15,subQ0,subQ10])],"isStart":false})})});}
            extrude(context, id + "F31", {"entities" : qUnion([Q0, Q1, Q2, Q3]), "operationType" : NewBodyOperationType.REMOVE, "oppositeDirection" : true, "depth" : 10.16 * mm});
        }
        {
            var Q0;
            {var subQ0=makeQuery(id+"F15.opExtrude","SWEPT_FACE",FACE,{"disambiguationData":[OSD([sQuery(id+"F14.wireOp",EDGE,"E61")])]});var subQ1=sQuery(id+"F9.wireOp",EDGE,"E51");var subQ2=makeQuery(id+"F12.opExtrude","SWEPT_FACE",FACE,{"disambiguationData":[OSD([subQ1])]});var subQ4=sQuery(id+"F1.wireOp",EDGE,"E0");var subQ6=sQuery(id+"F1.wireOp",EDGE,"E36");var subQ8=sQuery(id+"F1.wireOp",EDGE,"E37");var subQ10=makeQuery(id+"F11.opExtrude","SWEPT_FACE",FACE,{"disambiguationData":[OSD([sQuery(id+"F8.wireOp",EDGE,"E46")])]});var subQ17=sQuery(id+"F27.wireOp",EDGE,"E130");var subQ22=makeQuery(id+"F13.opExtrude","SWEPT_FACE",FACE,{"disambiguationData":[OSD([sQuery(id+"F10.wireOp",EDGE,"E56")])]});var subQ23=sQuery(id+"F1.wireOp",EDGE,"E41.trimOffspring");var subQ24=sQuery(id+"F1.wireOp",EDGE,"E40");var subQ25=sQuery(id+"F1.wireOp",EDGE,"E39.trimOffspring");var subQ26=sQuery(id+"F1.wireOp",EDGE,"E38");var subQ27=sQuery(id+"F1.wireOp",EDGE,"E35");var subQ28=sQuery(id+"F1.wireOp",EDGE,"E32");var subQ29=sQuery(id+"F1.wireOp",EDGE,"E28");var subQ30=sQuery(id+"F1.wireOp",EDGE,"E15.trimOffspring");var subQ31=sQuery(id+"F1.wireOp",EDGE,"E12");var subQ32=sQuery(id+"F1.wireOp",EDGE,"E11.trimOffspring");var subQ33=sQuery(id+"F1.wireOp",EDGE,"E1");var subQ34=makeQuery(id+"F2.opExtrude","CAP_FACE",FACE,{"disambiguationData":[OSD([subQ4,subQ33,subQ32,subQ31,subQ30,subQ29,subQ28,subQ27,subQ6,subQ26,subQ25,subQ24,subQ23])],"isStart":false});var subQ51=sQuery(id+"F9.wireOp",EDGE,"E47");var subQ53=makeQuery(id+"F3.opExtrude","SWEPT_FACE",FACE,{"disambiguationData":[OSD([subQ6])]});var subQ60=makeQuery(id+"F3.opExtrude","SWEPT_FACE",FACE,{"disambiguationData":[OSD([subQ27])]});var subQ62=makeQuery(id+"F6.boolean.opBoolean","SPLIT",FACE,{"disambiguationData":[TD([subQ60])],"derivedFrom":subQ34});var subQ63=makeQuery(id+"F3.opExtrude","SWEPT_FACE",FACE,{"disambiguationData":[OSD([subQ28])]});var subQ66=makeQuery(id+"F3.opExtrude","SWEPT_FACE",FACE,{"disambiguationData":[OSD([subQ29])]});var subQ67=makeQuery(id+"F6.boolean.opBoolean","SPLIT",FACE,{"disambiguationData":[TD([subQ66])],"derivedFrom":subQ34});Q0=makeQuery(id+"F29.boolean.opBoolean","SPLIT",FACE,{"disambiguationData":[TD([makeQuery(id+"F18.opExtrude","SWEPT_FACE",FACE,{"disambiguationData":[OSD([subQ8])]})])],"derivedFrom":makeQuery(id+"F28.boolean.opBoolean","MERGE",FACE,{"derivedFrom":[makeQuery(id+"F26.boolean.opBoolean","MERGE",FACE,{"derivedFrom":[makeQuery(id+"F18.boolean.opBoolean","SPLIT",FACE,{"disambiguationData":[TD([makeQuery(id+"F12.boolean.opBoolean","COPY",FACE,{"derivedFrom":makeQuery(id+"F12.opExtrude","SWEPT_FACE",FACE,{"disambiguationData":[OSD([subQ51])]})})])],"derivedFrom":makeQuery(id+"F15.boolean.opBoolean","MERGE",FACE,{"derivedFrom":[makeQuery(id+"F13.boolean.opBoolean","MERGE",FACE,{"derivedFrom":[makeQuery(id+"F11.boolean.opBoolean","MERGE",FACE,{"derivedFrom":[makeQuery(id+"F7.boolean.opBoolean","SPLIT",FACE,{"disambiguationData":[TD([subQ66])],"derivedFrom":subQ67}),makeQuery(id+"F7.boolean.opBoolean","SPLIT",FACE,{"disambiguationData":[TD([subQ63])],"derivedFrom":subQ67}),subQ10]}),makeQuery(id+"F12.boolean.opBoolean","MERGE",FACE,{"derivedFrom":[makeQuery(id+"F7.boolean.opBoolean","SPLIT",FACE,{"disambiguationData":[TD([subQ60])],"derivedFrom":subQ62}),makeQuery(id+"F7.boolean.opBoolean","SPLIT",FACE,{"disambiguationData":[TD([subQ53])],"derivedFrom":subQ62}),subQ2]}),subQ22]}),subQ0]})}),makeQuery(id+"F26.opExtrude","SWEPT_FACE",FACE,{"disambiguationData":[OSD([sQuery(id+"F25.wireOp",EDGE,"E125")])]})]}),makeQuery(id+"F28.opExtrude","SWEPT_FACE",FACE,{"disambiguationData":[OSD([subQ17])]})]})});}
            var sketch = newSketch(context, id + "F32", { "sketchPlane" : qUnion([Q0])});
            skLineSegment(sketch, "E134", {"start": v(43.89, -19.86) * mm, "end": v(43.89, -25.59) * mm});
            skLineSegment(sketch, "E135", {"start": v(43.89, -25.59) * mm, "end": v(54.72, -25.59) * mm});
            skLineSegment(sketch, "E136", {"start": v(54.72, -25.59) * mm, "end": v(48.32, -19) * mm});
            skLineSegment(sketch, "E137", {"start": v(43.89, 19.86) * mm, "end": v(55.83, 19.86) * mm});
            skLineSegment(sketch, "E138", {"start": v(55.83, 19.86) * mm, "end": v(53.72, 36.87) * mm});
            skLineSegment(sketch, "E139", {"start": v(43.89, 19.86) * mm, "end": v(43.89, 42.18) * mm});
            skLineSegment(sketch, "E140", {"start": v(43.89, 42.18) * mm, "end": v(53.72, 36.87) * mm});
            skLineSegment(sketch, "E141", {"start": v(-42.64, 34.63) * mm, "end": v(-42.64, 19.86) * mm});
            skLineSegment(sketch, "E142", {"start": v(-42.64, 19.86) * mm, "end": v(-45.34, 15.95) * mm});
            skLineSegment(sketch, "E143", {"start": v(-45.34, 15.95) * mm, "end": v(-51.25, 18.31) * mm});
            skLineSegment(sketch, "E144", {"start": v(-51.25, 18.31) * mm, "end": v(-42.64, 34.63) * mm});
            skLineSegment(sketch, "E145", {"start": v(-42.64, -19.86) * mm, "end": v(-42.64, -33.8) * mm});
            skLineSegment(sketch, "E146", {"start": v(-42.64, -33.8) * mm, "end": v(-52.6, -19) * mm});
            skLineSegment(sketch, "E147", {"start": v(-52.6, -19) * mm, "end": v(-43.88, -18.33) * mm});
            skLineSegment(sketch, "E148", {"start": v(-43.88, -18.33) * mm, "end": v(-42.64, -19.86) * mm});
            skLineSegment(sketch, "E149", {"start": v(43.89, -19.86) * mm, "end": v(45.92, -16.92) * mm});
            skLineSegment(sketch, "E150", {"start": v(45.92, -16.92) * mm, "end": v(48.32, -19) * mm});
            skSolve(sketch);
        }
        {
            var Q0;
            Q0 = qSketchRegion(id + "F32", true);
            extrude(context, id + "F33", {"entities" : qUnion([Q0]), "operationType" : NewBodyOperationType.REMOVE, "oppositeDirection" : true, "depth" : 25.4 * mm});
        }
        {
            var Q0;
            {var subQ0=sQuery(id+"F1.wireOp",EDGE,"E21");var subQ1=sQuery(id+"F1.wireOp",EDGE,"E18");var subQ2=sQuery(id+"F1.wireOp",EDGE,"E5");var subQ3=sQuery(id+"F1.wireOp",EDGE,"E0");var subQ4=sQuery(id+"F1.wireOp",EDGE,"E22");var subQ5=sQuery(id+"F1.wireOp",EDGE,"E17");var subQ6=sQuery(id+"F1.wireOp",EDGE,"E4");var subQ7=sQuery(id+"F1.wireOp",EDGE,"E19");var subQ8=sQuery(id+"F1.wireOp",EDGE,"E6");var subQ9=sQuery(id+"F1.wireOp",EDGE,"E20");var subQ10=sQuery(id+"F1.wireOp",EDGE,"E7");var subQ11=sQuery(id+"F1.wireOp",EDGE,"E3");Q0=makeQuery(id+"F18.boolean.opBoolean","MERGE",FACE,{"derivedFrom":[makeQuery(id+"F7.boolean.opBoolean","MERGE",FACE,{"derivedFrom":[makeQuery(id+"F6.boolean.opBoolean","MERGE",FACE,{"derivedFrom":[makeQuery(id+"F5.opExtrude","CAP_FACE",FACE,{"disambiguationData":[OSD([subQ11,sQuery(id+"F1.wireOp",EDGE,"E14")])],"isStart":false}),makeQuery(id+"F6.opExtrude","CAP_FACE",FACE,{"disambiguationData":[OSD([subQ3,subQ6,subQ2,subQ8,subQ10,subQ5,subQ1])],"isStart":false})]}),makeQuery(id+"F7.opExtrude","CAP_FACE",FACE,{"disambiguationData":[OSD([subQ3,subQ11,subQ5,subQ7,subQ4,sQuery(id+"F1.wireOp",EDGE,"E23")])],"isStart":false}),makeQuery(id+"F7.opExtrude","CAP_FACE",FACE,{"disambiguationData":[OSD([subQ3,subQ11,subQ1,subQ9,subQ0,sQuery(id+"F1.wireOp",EDGE,"E26")])],"isStart":false})]}),makeQuery(id+"F18.opExtrude","CAP_FACE",FACE,{"disambiguationData":[OSD([subQ3,subQ10,subQ1,subQ9,sQuery(id+"F1.wireOp",EDGE,"E34")])],"isStart":false}),makeQuery(id+"F18.opExtrude","CAP_FACE",FACE,{"disambiguationData":[OSD([subQ3,subQ8,subQ5,subQ7,sQuery(id+"F1.wireOp",EDGE,"E33")])],"isStart":false}),makeQuery(id+"F18.opExtrude","CAP_FACE",FACE,{"disambiguationData":[OSD([subQ3,subQ6,subQ5,subQ4,sQuery(id+"F1.wireOp",EDGE,"E31")])],"isStart":false}),makeQuery(id+"F18.opExtrude","CAP_FACE",FACE,{"disambiguationData":[OSD([subQ3,subQ2,subQ1,subQ0,sQuery(id+"F1.wireOp",EDGE,"E37")])],"isStart":false})]});}
            var sketch = newSketch(context, id + "F34", { "sketchPlane" : qUnion([Q0])});
            skLineSegment(sketch, "E151", {"start": v(-1.27, 6.53) * mm, "end": v(-1.27, 0.5) * mm});
            skLineSegment(sketch, "E152", {"start": v(-1.27, -6.04) * mm, "end": v(1.27, -6.04) * mm});
            skLineSegment(sketch, "E153", {"start": v(1.27, -6.04) * mm, "end": v(1.27, -0.56) * mm});
            skLineSegment(sketch, "E154", {"start": v(1.27, 6.53) * mm, "end": v(-1.27, 6.53) * mm});
            skLineSegment(sketch, "E155.trimOffspring", {"start": v(-1.27, -0.56) * mm, "end": v(-1.27, -6.04) * mm});
            skLineSegment(sketch, "E156.trimOffspring", {"start": v(1.27, 0.5) * mm, "end": v(1.27, 6.53) * mm});
            skLineSegment(sketch, "E157", {"start": v(-1.27, 0.5) * mm, "end": v(-1.27, -0.56) * mm});
            skLineSegment(sketch, "E158", {"start": v(1.27, 0.5) * mm, "end": v(1.27, -0.56) * mm});
            skSolve(sketch);
        }
        {
            var Q0;
            Q0 = qSketchRegion(id + "F34", true);
            extrude(context, id + "F35", {"entities" : qUnion([Q0]), "operationType" : NewBodyOperationType.REMOVE, "oppositeDirection" : true, "depth" : 47 * mm});
        }
    });
